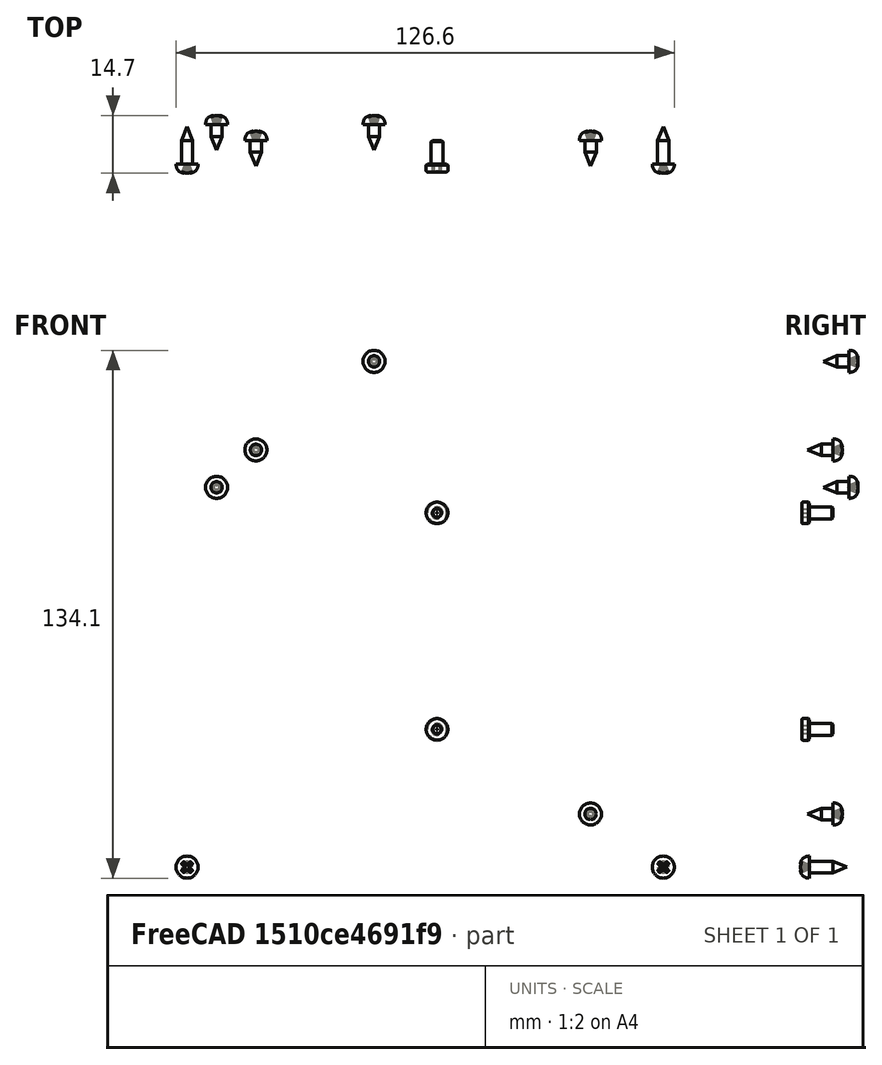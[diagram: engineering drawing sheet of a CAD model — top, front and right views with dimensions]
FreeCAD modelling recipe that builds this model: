
FCSTD DOCUMENT  (FreeCAD 1.0R39319 (Git))
Label: Assy_Stack_Module_PSU
License: All rights reserved
LicenseURL: https://en.wikipedia.org/wiki/All_rights_reserved
objects: TechDraw::DrawViewBalloon×18, App::Link×17, Part::FeaturePython×8, TechDraw::DrawProjGroupItem×6, TechDraw::DrawViewDimension×4, App::DocumentObjectGroup×3, TechDraw::DrawSVGTemplate×2, TechDraw::DrawPage×2, PartDesign::CoordinateSystem×1, App::FeaturePython×1, Spreadsheet::Sheet×1, TechDraw::DrawViewSpreadsheet×1, TechDraw::DrawViewAnnotation×1, App::Part×1, TechDraw::DrawProjGroup×1
note: 17 computed .brp shape members not serialized (recipe doc carries the construction recipe); baked Part::Feature solids carry a one-line shape summary decoded from their .brp
EXTERNAL_REF file=../../Part/Print/Stack_Module_PSU_vent.FCStd obj=LCS_1
EXTERNAL_REF file=../../Part/Print/Stack_Module_PSU_vent.FCStd obj=Part
EXTERNAL_REF file=Assy_M5_rod.FCStd obj=LCS_Origin
EXTERNAL_REF file=Assy_M5_rod.FCStd obj=Assembly
EXTERNAL_REF file=../../Part/Print/Stack_Module_PSU_vent.FCStd obj=LCS_2
EXTERNAL_REF file=../../Part/Print/Stack_Module_PSU_vent.FCStd obj=LCS_3
EXTERNAL_REF file=../../Part/Print/Stack_Module_PSU_vent.FCStd obj=LCS_4
EXTERNAL_REF file=../../Part/Print/Spacer.FCStd obj=LCS_1
EXTERNAL_REF file=../../Part/Print/Stack_Module_PSU_vent.FCStd obj=spacer_att
EXTERNAL_REF file=../../Part/Print/Spacer.FCStd obj=Part
EXTERNAL_REF file=../../Part/Print/Stack_Module_PSU_vent.FCStd obj=spacer_att_2
EXTERNAL_REF file=../../Part/Print/Stack_Module_PSU_vent.FCStd obj=spacer_att_3
EXTERNAL_REF file=../../Part/Print/Stack_Module_PSU_vent.FCStd obj=spacer_att_004
EXTERNAL_REF file=../../Part/Purchase/LRS-75.FCStd obj=stack_attach
EXTERNAL_REF file=../../Part/Print/Stack_Module_PSU_vent.FCStd obj=PSU_attachment
EXTERNAL_REF file=../../Part/Purchase/LRS-75.FCStd obj=LRS_75_ASM
EXTERNAL_REF file=Assy_Foot.FCStd obj=LCS_Origin
EXTERNAL_REF file=Assy_Foot.FCStd obj=Assembly
EXTERNAL_REF file=../../Part/Print/Ambient_LED_Screen.FCStd obj=stack_att
EXTERNAL_REF file=../../Part/Print/Stack_Module_PSU_vent.FCStd obj=screen_attachment
EXTERNAL_REF file=../../Part/Print/Ambient_LED_Screen.FCStd obj=Part
EXTERNAL_REF file=../../Part/Print/LinePower_Cover.FCStd obj=stack_att
EXTERNAL_REF file=../../Part/Print/Stack_Module_PSU_vent.FCStd obj=linecover_att
EXTERNAL_REF file=../../Part/Print/LinePower_Cover.FCStd obj=Part
EXTERNAL_REF file=../../Part/Print/Ambient_LED_Visor.FCStd obj=LCS_1
EXTERNAL_REF file=../../Part/Print/Ambient_LED_Visor.FCStd obj=Part

FEATURE [App::DocumentObjectGroup] Parts
FEATURE [PartDesign::CoordinateSystem] LCS_Origin
  AttacherType = Attacher::AttachEngine3D
  AttachmentSupport = -> [X_Axis]
  MapMode = 2
FEATURE [App::DocumentObjectGroup] Constraints
FEATURE [App::FeaturePython] Variables  # WARN: FeaturePython — macro-defined, semantics opaque (R4)
  Type = App::PropertyContainer
FEATURE [App::DocumentObjectGroup] Configurations
FEATURE [App::Link] Stack_Module_PSU_vent
  AttachedBy = #LCS_1
  AttachedTo = Parent Assembly#LCS_Origin
  AttachmentOffset = pos=(0,0,0) rot=(-0.57735,-0.57735,0.57735;4.18879rad)
  LinkPlacement = pos=(66.5,3.42e-14,53.5) rot=(0,0,1;3.14159rad)
  LinkedObject = -> <external ../../Part/Print/Stack_Module_PSU_vent.FCStd>#Part
  Placement = pos=(66.5,3.42e-14,53.5) rot=(0,0,1;3.14159rad)
  SolverId = Asm4EE
  expr: Placement = LCS_Origin.Placement * AttachmentOffset * Stack_Module_PSU_vent#LCS_1.Placement ^ -1
FEATURE [App::Link] Assy_M5_rod
  AttachedBy = #LCS_Origin
  AttachedTo = Stack_Module_PSU_vent#LCS_1
  AttachmentOffset = pos=(0,0,2) rot=(1,0,0;3.14159rad)
  LinkPlacement = pos=(1.49e-14,-2,1.47e-14) rot=(0.57735,-0.57735,-0.57735;4.18879rad)
  LinkedObject = -> <external Assy_M5_rod.FCStd>#Assembly
  Placement = pos=(1.49e-14,-2,1.47e-14) rot=(0.57735,-0.57735,-0.57735;4.18879rad)
  SolverId = Asm4EE
  expr: Placement = Stack_Module_PSU_vent.Placement * Stack_Module_PSU_vent#LCS_1.Placement * AttachmentOffset * Assy_M5_rod#LCS_Origin.Placement ^ -1
FEATURE [App::Link] Assy_M5_rod001
  AttachedBy = #LCS_Origin
  AttachedTo = Stack_Module_PSU_vent#LCS_2
  AttachmentOffset = pos=(0,0,2) rot=(1,0,0;3.14159rad)
  LinkPlacement = pos=(3,-2,116) rot=(0.57735,-0.57735,-0.57735;4.18879rad)
  LinkedObject = -> <external Assy_M5_rod.FCStd>#Assembly
  Placement = pos=(3,-2,116) rot=(0.57735,-0.57735,-0.57735;4.18879rad)
  SolverId = Asm4EE
  expr: Placement = Stack_Module_PSU_vent.Placement * Stack_Module_PSU_vent#LCS_2.Placement * AttachmentOffset * Assy_M5_rod#LCS_Origin.Placement ^ -1
FEATURE [App::Link] Assy_M5_rod002
  AttachedBy = #LCS_Origin
  AttachedTo = Stack_Module_PSU_vent#LCS_3
  AttachmentOffset = pos=(0,0,-2) rot=(0,0,1;0rad)
  LinkPlacement = pos=(133,-2,2.89e-14) rot=(-0.57735,0.57735,0.57735;2.0944rad)
  LinkedObject = -> <external Assy_M5_rod.FCStd>#Assembly
  Placement = pos=(133,-2,2.89e-14) rot=(-0.57735,0.57735,0.57735;2.0944rad)
  SolverId = Asm4EE
  expr: Placement = Stack_Module_PSU_vent.Placement * Stack_Module_PSU_vent#LCS_3.Placement * AttachmentOffset * Assy_M5_rod#LCS_Origin.Placement ^ -1
FEATURE [App::Link] Assy_M5_rod003
  AttachedBy = #LCS_Origin
  AttachedTo = Stack_Module_PSU_vent#LCS_4
  AttachmentOffset = pos=(0,0,-2) rot=(0,0,1;0rad)
  LinkPlacement = pos=(130,-2,116) rot=(-0.57735,0.57735,0.57735;2.0944rad)
  LinkedObject = -> <external Assy_M5_rod.FCStd>#Assembly
  Placement = pos=(130,-2,116) rot=(-0.57735,0.57735,0.57735;2.0944rad)
  SolverId = Asm4EE
  expr: Placement = Stack_Module_PSU_vent.Placement * Stack_Module_PSU_vent#LCS_4.Placement * AttachmentOffset * Assy_M5_rod#LCS_Origin.Placement ^ -1
FEATURE [App::Link] Spacer
  AttachedBy = #LCS_1
  AttachedTo = Stack_Module_PSU_vent#spacer_att
  LinkPlacement = pos=(0,35.25,7.1e-15) rot=(0,0.707107,0.707107;3.14159rad)
  LinkedObject = -> <external ../../Part/Print/Spacer.FCStd>#Part
  Placement = pos=(0,35.25,7.1e-15) rot=(0,0.707107,0.707107;3.14159rad)
  SolverId = Asm4EE
  expr: Placement = Stack_Module_PSU_vent.Placement * Stack_Module_PSU_vent#spacer_att.Placement * AttachmentOffset * Spacer#LCS_1.Placement ^ -1
FEATURE [App::Link] Spacer001
  AttachedBy = #LCS_1
  AttachedTo = Stack_Module_PSU_vent#spacer_att_2
  LinkPlacement = pos=(3,35.25,116) rot=(0,0.707107,0.707107;3.14159rad)
  LinkedObject = -> <external ../../Part/Print/Spacer.FCStd>#Part
  Placement = pos=(3,35.25,116) rot=(0,0.707107,0.707107;3.14159rad)
  SolverId = Asm4EE
  expr: Placement = Stack_Module_PSU_vent.Placement * Stack_Module_PSU_vent#spacer_att_2.Placement * AttachmentOffset * Spacer#LCS_1.Placement ^ -1
FEATURE [App::Link] Spacer002
  AttachedBy = #LCS_1
  AttachedTo = Stack_Module_PSU_vent#spacer_att_3
  AttachmentOffset = pos=(0,0,0) rot=(0,1,0;3.14159rad)
  LinkPlacement = pos=(130,35.25,116) rot=(1,0,0;4.71239rad)
  LinkedObject = -> <external ../../Part/Print/Spacer.FCStd>#Part
  Placement = pos=(130,35.25,116) rot=(1,0,0;4.71239rad)
  SolverId = Asm4EE
  expr: Placement = Stack_Module_PSU_vent.Placement * Stack_Module_PSU_vent#spacer_att_3.Placement * AttachmentOffset * Spacer#LCS_1.Placement ^ -1
FEATURE [App::Link] Spacer003
  AttachedBy = #LCS_1
  AttachedTo = Stack_Module_PSU_vent#spacer_att_004
  AttachmentOffset = pos=(0,0,0) rot=(0,1,0;3.14159rad)
  LinkPlacement = pos=(133,35.25,2.13e-14) rot=(1,0,0;4.71239rad)
  LinkedObject = -> <external ../../Part/Print/Spacer.FCStd>#Part
  Placement = pos=(133,35.25,2.13e-14) rot=(1,0,0;4.71239rad)
  SolverId = Asm4EE
  expr: Placement = Stack_Module_PSU_vent.Placement * Stack_Module_PSU_vent#spacer_att_004.Placement * AttachmentOffset * Spacer#LCS_1.Placement ^ -1
FEATURE [App::Link] LRS_75_ASM  label="LRS-75_ASM"
  AttachedBy = #stack_attach
  AttachedTo = Stack_Module_PSU_vent#PSU_attachment
  LinkPlacement = pos=(318.201,10.6,-201.167) rot=(-0.577138,0.577457,0.577457;2.09471rad)
  LinkedObject = -> <external ../../Part/Purchase/LRS-75.FCStd>#LRS_75_ASM
  Placement = pos=(318.201,10.6,-201.167) rot=(-0.577138,0.577457,0.577457;2.09471rad)
  SolverId = Asm4EE
  expr: Placement = Stack_Module_PSU_vent.Placement * Stack_Module_PSU_vent#PSU_attachment.Placement * AttachmentOffset * LRS_75#stack_attach.Placement ^ -1
FEATURE [App::Link] Assy_Foot
  AttachedBy = #LCS_Origin
  AttachedTo = Stack_Module_PSU_vent#LCS_1
  AttachmentOffset = pos=(0,0,5) rot=(0,1,0;3.14159rad)
  LinkPlacement = pos=(1.59e-14,-5,1.53e-14) rot=(0.57735,0.57735,0.57735;4.18879rad)
  LinkedObject = -> <external Assy_Foot.FCStd>#Assembly
  Placement = pos=(1.59e-14,-5,1.53e-14) rot=(0.57735,0.57735,0.57735;4.18879rad)
  SolverId = Asm4EE
  expr: Placement = Stack_Module_PSU_vent.Placement * Stack_Module_PSU_vent#LCS_1.Placement * AttachmentOffset * Assy_Foot#LCS_Origin.Placement ^ -1
FEATURE [App::Link] Assy_Foot001
  AttachedBy = #LCS_Origin
  AttachedTo = Stack_Module_PSU_vent#LCS_2
  AttachmentOffset = pos=(0,0,5) rot=(0,1,0;3.14159rad)
  LinkPlacement = pos=(3,-5,116) rot=(0.57735,0.57735,0.57735;4.18879rad)
  LinkedObject = -> <external Assy_Foot.FCStd>#Assembly
  Placement = pos=(3,-5,116) rot=(0.57735,0.57735,0.57735;4.18879rad)
  SolverId = Asm4EE
  expr: Placement = Stack_Module_PSU_vent.Placement * Stack_Module_PSU_vent#LCS_2.Placement * AttachmentOffset * Assy_Foot#LCS_Origin.Placement ^ -1
FEATURE [App::Link] Assy_Foot002
  AttachedBy = #LCS_Origin
  AttachedTo = Stack_Module_PSU_vent#LCS_3
  AttachmentOffset = pos=(0,0,-5) rot=(0,0,1;0rad)
  LinkPlacement = pos=(133,-5,2.95e-14) rot=(-0.57735,0.57735,0.57735;2.0944rad)
  LinkedObject = -> <external Assy_Foot.FCStd>#Assembly
  Placement = pos=(133,-5,2.95e-14) rot=(-0.57735,0.57735,0.57735;2.0944rad)
  SolverId = Asm4EE
  expr: Placement = Stack_Module_PSU_vent.Placement * Stack_Module_PSU_vent#LCS_3.Placement * AttachmentOffset * Assy_Foot#LCS_Origin.Placement ^ -1
FEATURE [App::Link] Assy_Foot003
  AttachedBy = #LCS_Origin
  AttachedTo = Stack_Module_PSU_vent#LCS_4
  AttachmentOffset = pos=(0,0,-5) rot=(0,0,1;0rad)
  LinkPlacement = pos=(130,-5,116) rot=(-0.57735,0.57735,0.57735;2.0944rad)
  LinkedObject = -> <external Assy_Foot.FCStd>#Assembly
  Placement = pos=(130,-5,116) rot=(-0.57735,0.57735,0.57735;2.0944rad)
  SolverId = Asm4EE
  expr: Placement = Stack_Module_PSU_vent.Placement * Stack_Module_PSU_vent#LCS_4.Placement * AttachmentOffset * Assy_Foot#LCS_Origin.Placement ^ -1
FEATURE [App::Link] Ambient_LED_Screen
  AttachedBy = #stack_att
  AttachedTo = Stack_Module_PSU_vent#screen_attachment
  LinkPlacement = pos=(66.5,3,-9) rot=(1,0,0;4.71239rad)
  LinkedObject = -> <external ../../Part/Print/Ambient_LED_Screen.FCStd>#Part
  Placement = pos=(66.5,3,-9) rot=(1,0,0;4.71239rad)
  SolverId = Asm4EE
  expr: Placement = Stack_Module_PSU_vent.Placement * Stack_Module_PSU_vent#screen_attachment.Placement * AttachmentOffset * Ambient_LED_Screen#stack_att.Placement ^ -1
FEATURE [App::Link] LinePower_Cover
  AttachedBy = #stack_att
  AttachedTo = Stack_Module_PSU_vent#linecover_att
  AttachmentOffset = pos=(0,0,0) rot=(0,0,1;3.14159rad)
  LinkPlacement = pos=(10.5,4,120.5) rot=(1,0,0;4.71239rad)
  LinkedObject = -> <external ../../Part/Print/LinePower_Cover.FCStd>#Part
  Placement = pos=(10.5,4,120.5) rot=(1,0,0;4.71239rad)
  SolverId = Asm4EE
  expr: Placement = Stack_Module_PSU_vent.Placement * Stack_Module_PSU_vent#linecover_att.Placement * AttachmentOffset * LinePower_Cover#stack_att.Placement ^ -1
FEATURE [Part::FeaturePython] Screw  label="ST2.9x6.5-Screw013"  # WARN: FeaturePython — macro-defined, semantics opaque (R4)
  BaseObject = -> Stack_Module_PSU_vent [Body.LinearPattern005.Edge4238]
  Diameter = 2
  Invert = false
  LeftHanded = false
  Length = 0
  LengthCustom = 6.5
  MatchOuter = false
  Offset = 2
  OffsetAngle = 0
  Placement = pos=(108.5,6,1.5) rot=(-1,0,0;1.5708rad)
  Thread = false
  Type = 81
FEATURE [Part::FeaturePython] Screw002  label="ST2.9x6.5-Screw"  # WARN: FeaturePython — macro-defined, semantics opaque (R4)
  BaseObject = -> Stack_Module_PSU_vent [Body.LinearPattern005.Edge4103]
  Diameter = 2
  Invert = false
  LeftHanded = false
  Length = 0
  LengthCustom = 6.5
  MatchOuter = false
  Offset = 2
  OffsetAngle = 0
  Placement = pos=(23.5,6,94) rot=(-1,0,0;1.5708rad)
  Thread = false
  Type = 81
FEATURE [Part::FeaturePython] Screw003  label="ST2.9x6.5-Screw014"  # WARN: FeaturePython — macro-defined, semantics opaque (R4)
  BaseObject = -> LinePower_Cover [Body.Fillet007.Edge85]
  Diameter = 2
  Invert = false
  LeftHanded = false
  Length = 0
  LengthCustom = 6.5
  MatchOuter = false
  OffsetAngle = 0
  Placement = pos=(53.5,10,116.5) rot=(-1,0,0;1.5708rad)
  Thread = false
  Type = 81
FEATURE [Part::FeaturePython] Screw004  label="ST2.9x6.5-Screw015"  # WARN: FeaturePython — macro-defined, semantics opaque (R4)
  BaseObject = -> LinePower_Cover [Body.Fillet007.Edge96]
  Diameter = 2
  Invert = false
  LeftHanded = false
  Length = 0
  LengthCustom = 6.5
  MatchOuter = false
  OffsetAngle = 0
  Placement = pos=(13.5,10,84.5) rot=(-1,0,0;1.5708rad)
  Thread = false
  Type = 81
FEATURE [Part::FeaturePython] Screw005  label="M3x6-Screw"  # WARN: FeaturePython — macro-defined, semantics opaque (R4)
  BaseObject = -> Stack_Module_PSU_vent [Body.LinearPattern005.Edge1214]
  Diameter = 1
  Invert = true
  LeftHanded = false
  Length = 1
  LengthCustom = 6
  MatchOuter = false
  OffsetAngle = 0
  Placement = pos=(69.5,2.01e-14,23) rot=(1,0,0;1.5708rad)
  Thread = false
  Type = 37
FEATURE [Part::FeaturePython] Screw006  label="M3x6-Screw001"  # WARN: FeaturePython — macro-defined, semantics opaque (R4)
  BaseObject = -> Stack_Module_PSU_vent [Body.LinearPattern005.Edge1213]
  Diameter = 1
  Invert = true
  LeftHanded = false
  Length = 1
  LengthCustom = 6
  MatchOuter = false
  OffsetAngle = 0
  Placement = pos=(69.5,4.1e-14,78) rot=(1,0,0;1.5708rad)
  Thread = false
  Type = 37
FEATURE [Part::FeaturePython] Screw007  label="ST2.9x9.5-Screw"  # WARN: FeaturePython — macro-defined, semantics opaque (R4)
  BaseObject = -> Stack_Module_PSU_vent [Body.LinearPattern005.Edge1216]
  Diameter = 2
  Invert = false
  LeftHanded = false
  Length = 1
  LengthCustom = 9.5
  MatchOuter = false
  OffsetAngle = 0
  Placement = pos=(127,2.26e-14,-12) rot=(1,0,0;1.5708rad)
  Thread = false
  Type = 81
FEATURE [Part::FeaturePython] Screw008  label="ST2.9x9.5-Screw001"  # WARN: FeaturePython — macro-defined, semantics opaque (R4)
  BaseObject = -> Stack_Module_PSU_vent [Body.LinearPattern005.Edge1215]
  Diameter = 2
  Invert = true
  LeftHanded = false
  Length = 1
  LengthCustom = 9.5
  MatchOuter = false
  OffsetAngle = 0
  Placement = pos=(6,-1.77e-14,-12) rot=(1,0,0;1.5708rad)
  Thread = false
  Type = 81
FEATURE [Spreadsheet::Sheet] Spreadsheet  label="BOM"
  cells = A1=12; B1=4; C1='M3x10 mm self-tapping screw; D1=' 5-16 mm; A2=11; B2=4; C2='M3x5 mm self-tapping screw; D2='5-6 mm; A3=10; B3=2; C3='M3x6 mm screw; D3='5-6 mm; A4=9; B4=3; C4='Wires; D4='-; A5=8; B5=1; C5='USB COB LED Strip Lights; D5='roughly 60 cm; A6=7; B6=1; C6='AC Power Inlet C14 with Fuse; D6='-; A7=6; B7=1; C7='Meanwell LRS-75-5; D7='-; A8=5; B8=4; C8='Spacer; D8='-; E8='PETG or PLA; A9=4; B9=1; C9='Ambient_LED_Visor; D9='-; E9='PETG or PLA; A10=3; B10=1; C10='LinePower_Cover; D10='-; E10='PETG or PLA; A11=2; B11=1; C11='Ambient_LED_Screen; D11='-; E11='PETG or PLA; A12=1; B12=1; C12='Stack_Module_PSU_vent; D12='-; E12='PETG or PLA; A13='Position; B13='Quantity; C13='Part; D13='Dimensions; E13='Material
FEATURE [TechDraw::DrawViewBalloon] Balloon
  BubbleShape = 0
  EndType = 0
  EndTypeScale = 1
  KinkLength = 5
  LockPosition = false
  OriginX = 74.9138
  OriginY = -16.347
  Rotation = 0
  ScaleType = 0
  ShapeScale = 1
  Text = 1
  TextWrapLen = -1
  X = 128.799
  Y = -72.3092
FEATURE [TechDraw::DrawViewBalloon] Balloon003
  BubbleShape = 0
  EndType = 0
  EndTypeScale = 1
  KinkLength = 5
  LockPosition = false
  OriginX = -3.65673
  OriginY = -43.3871
  Rotation = 0
  ScaleType = 0
  ShapeScale = 1
  Text = 4
  TextWrapLen = -1
  X = 130.81
  Y = -93.7522
FEATURE [TechDraw::DrawSVGTemplate] Template001
  EditableTexts = approval_person=GitHubPR; creator=Stefan; date_of_issue=19/3/2026; document_type=Assy_Stack_Module_PSU; general_tolerances=na; identification_number=na; language_code=EN; part_material=na; revision_index=AAA; scale=1 : 1; sheet_number=1 / 1; title=Assy_Stack_Module_PSU
  Height = 420
  Orientation = 1
  Template = <userpath>/Documents/PiTrac/3D Printed Parts/Enclosure Version 3/Assets/PiTrac_A2_Landscape_ISO5457_minimal.svg
  Width = 594
FEATURE [TechDraw::DrawViewSpreadsheet] Sheet001
  CellEnd = E13
  CellStart = A1
  Font = osifont
  LineWidth = 0.35
  LockPosition = false
  Rotation = 0
  ScaleType = 2
  Source = -> Spreadsheet
  Symbol = <blob: 14232 chars omitted>
  TextSize = 12
  X = 502.594
  Y = 129.653
FEATURE [TechDraw::DrawViewAnnotation] Annotation
  Font = osifont
  LineSpace = 100
  LockPosition = false
  MaxWidth = -1
  Rotation = 0
  ScaleType = 0
  Text = Not all parts are shown
  TextSize = 5
  TextStyle = 0
  X = 341.029
  Y = 39.0208
FEATURE [App::Link] Ambient_LED_Visor
  AttachedBy = #LCS_1
  AttachedTo = Parent Assembly#LCS_Origin
  AttachmentOffset = pos=(66.5,0,-46.5) rot=(0,0,1;3.14159rad)
  LinkPlacement = pos=(66.5,0,-46.5) rot=(0,0,1;3.14159rad)
  LinkedObject = -> <external ../../Part/Print/Ambient_LED_Visor.FCStd>#Part
  Placement = pos=(66.5,0,-46.5) rot=(0,0,1;3.14159rad)
  SolverId = Asm4EE
  expr: Placement = LCS_Origin.Placement * AttachmentOffset * Ambient_LED_Visor#LCS_1.Placement ^ -1
FEATURE [App::Part] Assembly  label="Assy_Stack_Module_PSU"
  AssemblyType = Part::Link
  Group = -> [LCS_Origin,Constraints,Variables,Configurations,Stack_Module_PSU_vent,Assy_M5_rod,Assy_M5_rod001,Assy_M5_rod002,Assy_M5_rod003,Spacer,Spacer001,Spacer002,Spacer003,LRS_75_ASM,Assy_Foot,Assy_Foot001,Assy_Foot002,Assy_Foot003,Ambient_LED_Screen,LinePower_Cover,Screw,Screw002,Screw003,Screw004,Screw005,Screw006,Screw007,Screw008,Ambient_LED_Visor]
  Origin = -> Origin
  Type = Assembly
FEATURE [TechDraw::DrawProjGroupItem] ProjItem  label="Top"
  CoarseView = false
  Direction = (0,1,0)
  Focus = 100
  HardHidden = false
  IsoCount = 0
  IsoHidden = false
  IsoVisible = false
  LockPosition = false
  Perspective = false
  Rotation = 0
  RotationVector = (1,0,0)
  ScaleType = 0
  ScrubCount = 1
  SeamHidden = false
  SeamVisible = false
  SmoothHidden = false
  SmoothVisible = true
  Source = -> [Assembly]
  Type = 4
  X = 0
  XDirection = (-1,0,-2e-16)
  Y = -133.625
FEATURE [TechDraw::DrawProjGroupItem] View002  label="Isometric View Scale 1:2"
  CoarseView = false
  Direction = (-0.57735,0.57735,-0.57735)
  Focus = 100
  HardHidden = false
  IsoCount = 0
  IsoHidden = false
  IsoVisible = false
  LockPosition = false
  Perspective = false
  Rotation = 0
  RotationVector = (1,0,0)
  Scale = 0.5
  ScaleType = 2
  ScrubCount = 1
  SeamHidden = false
  SeamVisible = false
  SmoothHidden = false
  SmoothVisible = true
  Source = -> [Assembly]
  Type = 0
  X = 336.894
  XDirection = (-0.707106,0,0.707106)
  Y = 114.331
FEATURE [TechDraw::DrawProjGroupItem] View003  label="Front001"
  CoarseView = false
  Direction = (0,0,-1)
  Focus = 100
  HardHidden = false
  IsoCount = 0
  IsoHidden = false
  IsoVisible = false
  LockPosition = true
  Perspective = false
  Rotation = 0
  RotationVector = (1,0,0)
  ScaleType = 2
  ScrubCount = 1
  SeamHidden = false
  SeamVisible = false
  SmoothHidden = false
  SmoothVisible = true
  Source = -> [Assembly]
  Type = 0
  X = 0
  XDirection = (-1,0,0)
  Y = 0
FEATURE [TechDraw::DrawProjGroupItem] ProjItem002  label="Top001"
  CoarseView = false
  Direction = (0,1,0)
  Focus = 100
  HardHidden = false
  IsoCount = 0
  IsoHidden = false
  IsoVisible = false
  LockPosition = false
  Perspective = false
  Rotation = 0
  RotationVector = (1,0,0)
  ScaleType = 0
  ScrubCount = 1
  SeamHidden = false
  SeamVisible = false
  SmoothHidden = false
  SmoothVisible = true
  Source = -> [Assembly]
  Type = 4
  X = 0
  XDirection = (-1,0,0)
  Y = -132.298
FEATURE [TechDraw::DrawProjGroupItem] ProjItem003  label="Left001"
  CoarseView = false
  Direction = (1,0,-1e-16)
  Focus = 100
  HardHidden = false
  IsoCount = 0
  IsoHidden = false
  IsoVisible = false
  LockPosition = false
  Perspective = false
  Rotation = 0
  RotationVector = (1,0,0)
  ScaleType = 0
  ScrubCount = 1
  SeamHidden = false
  SeamVisible = false
  SmoothHidden = false
  SmoothVisible = true
  Source = -> [Assembly]
  Type = 1
  X = 187
  XDirection = (-1e-16,0,-1)
  Y = 0
FEATURE [TechDraw::DrawProjGroup] ProjGroup001
  Anchor = -> View003
  AutoDistribute = true
  LockPosition = false
  ProjectionType = 0
  Rotation = 0
  ScaleType = 0
  Source = -> [Assembly]
  Views = -> [View003,ProjItem002,ProjItem003]
  X = 154.029
  Y = 330.521
  spacingX = 15
  spacingY = 15
FEATURE [TechDraw::DrawViewBalloon] Balloon007
  BubbleShape = 0
  EndType = 0
  EndTypeScale = 1
  KinkLength = 5
  LockPosition = false
  OriginX = -59
  OriginY = 9.65153
  Rotation = 0
  ScaleType = 0
  ShapeScale = 1
  SourceView = -> ProjItem002
  Text = 1
  TextWrapLen = -1
  X = -100
  Y = 25.036
FEATURE [TechDraw::DrawViewBalloon] Balloon008
  BubbleShape = 0
  EndType = 0
  EndTypeScale = 1
  KinkLength = 5
  LockPosition = false
  OriginX = -39.6652
  OriginY = 0.173159
  Rotation = 0
  ScaleType = 0
  ShapeScale = 1
  SourceView = -> View003
  Text = 2
  TextWrapLen = -1
  X = -100
  Y = 15.5576
FEATURE [TechDraw::DrawViewBalloon] Balloon009
  BubbleShape = 0
  EndType = 0
  EndTypeScale = 1
  KinkLength = 5
  LockPosition = false
  OriginX = 32.6431
  OriginY = 50.5032
  Rotation = 0
  ScaleType = 0
  ShapeScale = 1
  SourceView = -> ProjItem002
  Text = 3
  TextWrapLen = -1
  X = 100
  Y = 58.1951
FEATURE [TechDraw::DrawViewBalloon] Balloon010
  BubbleShape = 0
  EndType = 0
  EndTypeScale = 1
  KinkLength = 5
  LockPosition = false
  OriginX = -44.7952
  OriginY = -78.7316
  Rotation = 0
  ScaleType = 0
  ShapeScale = 1
  SourceView = -> ProjItem002
  Text = 4
  TextWrapLen = -1
  X = -100
  Y = -60.2701
FEATURE [TechDraw::DrawViewBalloon] Balloon011
  BubbleShape = 0
  EndType = 0
  EndTypeScale = 1
  KinkLength = 5
  LockPosition = false
  OriginX = -63.25
  OriginY = -48.5
  Rotation = 0
  ScaleType = 0
  ShapeScale = 1
  SourceView = -> ProjItem002
  Text = 5
  TextWrapLen = -1
  X = -100
  Y = -23.3716
FEATURE [TechDraw::DrawViewBalloon] Balloon012
  BubbleShape = 0
  EndType = 0
  EndTypeScale = 1
  KinkLength = 5
  LockPosition = false
  OriginX = -59.1546
  OriginY = 67.9396
  Rotation = 0
  ScaleType = 0
  ShapeScale = 1
  SourceView = -> ProjItem002
  Text = 5
  TextWrapLen = -1
  X = -100
  Y = 85
FEATURE [TechDraw::DrawViewBalloon] Balloon014
  BubbleShape = 0
  EndType = 0
  EndTypeScale = 1
  KinkLength = 5
  LockPosition = false
  OriginX = 62.9004
  OriginY = 64.8626
  Rotation = 0
  ScaleType = 0
  ShapeScale = 1
  SourceView = -> ProjItem002
  Text = 5
  TextWrapLen = -1
  X = 99.4872
  Y = 83.9743
FEATURE [TechDraw::DrawViewBalloon] Balloon015
  BubbleShape = 0
  EndType = 0
  EndTypeScale = 1
  KinkLength = 5
  LockPosition = false
  OriginX = 64.4389
  OriginY = -46.4229
  Rotation = 0
  ScaleType = 0
  ShapeScale = 1
  SourceView = -> ProjItem002
  Text = 5
  TextWrapLen = -1
  X = 100
  Y = -30.5256
FEATURE [TechDraw::DrawViewBalloon] Balloon016
  BubbleShape = 0
  EndType = 0
  EndTypeScale = 1
  KinkLength = 5
  LockPosition = false
  OriginX = 19.8222
  OriginY = 26.3999
  Rotation = 0
  ScaleType = 0
  ShapeScale = 1
  SourceView = -> ProjItem002
  Text = 6
  TextWrapLen = -1
  X = 100
  Y = 14.604
FEATURE [TechDraw::DrawViewBalloon] Balloon017
  BubbleShape = 0
  EndType = 0
  EndTypeScale = 1
  KinkLength = 5
  LockPosition = false
  OriginX = -26.75
  OriginY = -21.6518
  Rotation = 0
  ScaleType = 0
  ShapeScale = 1
  SourceView = -> ProjItem003
  Text = 10
  TextWrapLen = -1
  X = -42.1357
  Y = -49
FEATURE [TechDraw::DrawViewBalloon] Balloon018
  BubbleShape = 0
  EndType = 0
  EndTypeScale = 1
  KinkLength = 5
  LockPosition = false
  OriginX = 28.7257
  OriginY = -22.306
  Rotation = 0
  ScaleType = 0
  ShapeScale = 1
  SourceView = -> ProjItem003
  Text = 10
  TextWrapLen = -1
  X = 47.7
  Y = -49
FEATURE [TechDraw::DrawViewBalloon] Balloon019
  BubbleShape = 0
  EndType = 0
  EndTypeScale = 1
  KinkLength = 5
  LockPosition = false
  OriginX = -61.2512
  OriginY = -22.105
  Rotation = 0
  ScaleType = 0
  ShapeScale = 1
  SourceView = -> View003
  Text = 12
  TextWrapLen = -1
  X = -100
  Y = -14.4131
FEATURE [TechDraw::DrawViewBalloon] Balloon020
  BubbleShape = 0
  EndType = 0
  EndTypeScale = 1
  KinkLength = 5
  LockPosition = false
  OriginX = 61.2512
  OriginY = -22.105
  Rotation = 0
  ScaleType = 0
  ShapeScale = 1
  SourceView = -> View003
  Text = 12
  TextWrapLen = -1
  X = 122.791
  Y = -49
FEATURE [TechDraw::DrawViewBalloon] Balloon021
  BubbleShape = 0
  EndType = 0
  EndTypeScale = 1
  KinkLength = 5
  LockPosition = false
  OriginX = 12.4289
  OriginY = 67.795
  Rotation = 0
  ScaleType = 0
  ShapeScale = 1
  SourceView = -> ProjItem002
  Text = 11
  TextWrapLen = -1
  X = -100
  Y = 101.947
FEATURE [TechDraw::DrawViewBalloon] Balloon022
  BubbleShape = 0
  EndType = 0
  EndTypeScale = 1
  KinkLength = 5
  LockPosition = false
  OriginX = 53.6694
  OriginY = 36.1438
  Rotation = 0
  ScaleType = 0
  ShapeScale = 1
  SourceView = -> ProjItem002
  Text = 11
  TextWrapLen = -1
  X = 100
  Y = 36.7508
FEATURE [TechDraw::DrawViewBalloon] Balloon024
  BubbleShape = 0
  EndType = 0
  EndTypeScale = 1
  KinkLength = 5
  LockPosition = false
  OriginX = -40.504
  OriginY = -48.9784
  Rotation = 0
  ScaleType = 0
  ShapeScale = 1
  SourceView = -> ProjItem002
  Text = 11
  TextWrapLen = -1
  X = -100
  Y = -0.151091
FEATURE [TechDraw::DrawViewDimension] Dimension001
  AngleOverride = false
  Arbitrary = false
  ArbitraryTolerances = false
  BoxCorners = (2) [(-95,-22.2982,-1e-07),(95,22.2982,1e-07)]
  EqualTolerance = true
  ExtensionAngle = 0
  FormatSpec = %.2w
  FormatSpecOverTolerance = %+.2w
  FormatSpecUnderTolerance = %+.2w
  Inverted = false
  LineAngle = 0
  LockPosition = false
  MeasureType = 1
  OverTolerance = 0
  References2D = -> [ProjItem003]
  Rotation = 0
  ScaleType = 0
  TheoreticalExact = false
  Type = 1
  UnderTolerance = 0
  X = 0
  Y = 40
FEATURE [TechDraw::DrawViewDimension] Dimension002
  AngleOverride = false
  Arbitrary = false
  ArbitraryTolerances = false
  BoxCorners = (2) [(-77,-22.2982,-1e-07),(77,22.2982,1e-07)]
  EqualTolerance = true
  ExtensionAngle = 0
  FormatSpec = %.2w
  FormatSpecOverTolerance = %+.2w
  FormatSpecUnderTolerance = %+.2w
  Inverted = false
  LineAngle = 0
  LockPosition = false
  MeasureType = 1
  OverTolerance = 0
  References2D = -> [View003]
  Rotation = 0
  ScaleType = 0
  TheoreticalExact = false
  Type = 1
  UnderTolerance = 0
  X = 0
  Y = 40
FEATURE [TechDraw::DrawViewDimension] Dimension003
  AngleOverride = false
  Arbitrary = false
  ArbitraryTolerances = false
  BoxCorners = (2) [(-95,-22.2982,-1e-07),(95,22.2982,1e-07)]
  EqualTolerance = true
  ExtensionAngle = 0
  FormatSpec = %.2w
  FormatSpecOverTolerance = %+.2w
  FormatSpecUnderTolerance = %+.2w
  Inverted = false
  LineAngle = 0
  LockPosition = false
  MeasureType = 1
  OverTolerance = 0
  References2D = -> [ProjItem003]
  Rotation = 0
  ScaleType = 0
  TheoreticalExact = false
  Type = 0
  UnderTolerance = 0
  X = 131.873
  Y = 0.173159
FEATURE [TechDraw::DrawViewDimension] Dimension004
  AngleOverride = false
  Arbitrary = false
  ArbitraryTolerances = false
  BoxCorners = (2) [(-95,-22.2982,-1e-07),(95,22.2982,1e-07)]
  EqualTolerance = true
  ExtensionAngle = 0
  FormatSpec = %.2w
  FormatSpecOverTolerance = %+.2w
  FormatSpecUnderTolerance = %+.2w
  Inverted = false
  LineAngle = 0
  LockPosition = false
  MeasureType = 1
  OverTolerance = 0
  References2D = -> [ProjItem003]
  Rotation = 0
  ScaleType = 0
  TheoreticalExact = false
  Type = 2
  UnderTolerance = 0
  X = 160.232
  Y = 0.323159
FEATURE [TechDraw::DrawPage] Page001
  KeepUpdated = true
  NextBalloonIndex = 21
  ProjectionType = 0
  Template = -> Template001
  Views = -> [View002,Sheet001,ProjGroup001,Balloon007,Balloon008,Balloon009,Balloon010,Balloon011,Balloon012,Balloon014,Balloon015,Balloon016,Balloon017,Balloon018,Balloon019,Balloon020,Balloon021,Balloon022,Balloon024,Dimension001,Dimension002,Dimension003,Dimension004,Annotation]
FEATURE [TechDraw::DrawSVGTemplate] Template
  Height = 210
  Orientation = 1
  Template = C:/Program Files/FreeCAD 1.0/data/Mod/TechDraw/Templates/Default_Template_A4_Landscape.svg
  Width = 297
FEATURE [TechDraw::DrawProjGroupItem] View
  CoarseView = false
  Direction = (-0.57735,0.57735,-0.57735)
  Focus = 100
  HardHidden = false
  IsoCount = 0
  IsoHidden = false
  IsoVisible = false
  LockPosition = false
  Perspective = false
  Rotation = 0
  RotationVector = (1,0,0)
  ScaleType = 0
  ScrubCount = 1
  SeamHidden = false
  SeamVisible = false
  SmoothHidden = false
  SmoothVisible = true
  Source = -> [Assembly]
  Type = 0
  X = 148.5
  XDirection = (-0.707106,0,0.707106)
  Y = 105
FEATURE [TechDraw::DrawPage] Page
  KeepUpdated = true
  NextBalloonIndex = 1
  ProjectionType = 0
  Template = -> Template
  Views = -> [View]

RESOLVED EXTERNAL PARTS (link-assembly join: the EXTERNAL_REF files above that resolve inside this repo's crawl, each included once):
---- part ../../Part/Print/Ambient_LED_Screen.FCStd = doc fcstd_3e985b0e07c3 ----
FCSTD DOCUMENT  (FreeCAD 1.0R39319 (Git))
Label: Ambient_LED_Screen
License: All rights reserved
LicenseURL: https://en.wikipedia.org/wiki/All_rights_reserved
objects: Sketcher::SketchObject×7, PartDesign::Pocket×5, PartDesign::Pad×2, PartDesign::Chamfer×1, PartDesign::Mirrored×1, PartDesign::Body×1, PartDesign::CoordinateSystem×1, App::Part×1
note: 42 computed .brp shape members not serialized (recipe doc carries the construction recipe); baked Part::Feature solids carry a one-line shape summary decoded from their .brp

FEATURE [Sketcher::SketchObject] Sketch
  ArcFitTolerance = 1e-06
  AttachmentSupport = -> [XY_Plane001]
  FullyConstrained = true
  MakeInternals = false
  MapMode = 5
  sketch-geometry (20):
    g0: LineSegment StartX=52.3059 StartY=0 StartZ=0 EndX=60.5 EndY=0 EndZ=0
    g1: ArcOfCircle CenterX=60.5 CenterY=3 CenterZ=0 NormalX=0 NormalY=0 NormalZ=1 AngleXU=0 Radius=3 StartAngle=4.71239 EndAngle=8.29889
    g2: LineSegment StartX=59.2089 StartY=5.70795 StartZ=0 EndX=48.6478 EndY=0.672534 EndZ=0
    g3: ArcOfCircle CenterX=0 CenterY=4.259 CenterZ=0 NormalX=0 NormalY=0 NormalZ=1 AngleXU=0 Radius=7 StartAngle=4.71239 EndAngle=5.61581
    g4: ArcOfCircle CenterX=0 CenterY=4.259 CenterZ=0 NormalX=0 NormalY=0 NormalZ=1 AngleXU=0 Radius=5.5 StartAngle=4.71239 EndAngle=5.61581
    g5: LineSegment StartX=-1.3e-15 StartY=-2.741 StartZ=0 EndX=-1.3e-15 EndY=-1.241 EndZ=0
    g6: ArcOfCircle CenterX=10.9963 CenterY=-4.40596 CenterZ=0 NormalX=0 NormalY=0 NormalZ=1 AngleXU=0 Radius=7 StartAngle=0.667374 EndAngle=2.47422
    g7: ArcOfCircle CenterX=10.9963 CenterY=-4.40596 CenterZ=0 NormalX=0 NormalY=0 NormalZ=1 AngleXU=0 Radius=8.5 StartAngle=0.667374 EndAngle=2.47422
    g8: ArcOfCircle CenterX=21.9926 CenterY=4.259 CenterZ=0 NormalX=0 NormalY=0 NormalZ=1 AngleXU=0 Radius=5.5 StartAngle=3.80897 EndAngle=5.61581
    g9: ArcOfCircle CenterX=21.9926 CenterY=4.259 CenterZ=0 NormalX=0 NormalY=0 NormalZ=1 AngleXU=0 Radius=7 StartAngle=3.80897 EndAngle=5.61581
    g10: ArcOfCircle CenterX=32.9889 CenterY=-4.40596 CenterZ=0 NormalX=0 NormalY=0 NormalZ=1 AngleXU=0 Radius=8.5 StartAngle=0.667374 EndAngle=2.47422
    g11: ArcOfCircle CenterX=32.9889 CenterY=-4.40596 CenterZ=0 NormalX=0 NormalY=0 NormalZ=1 AngleXU=0 Radius=7 StartAngle=0.667374 EndAngle=2.47422
    g12: ArcOfCircle CenterX=43.9852 CenterY=4.259 CenterZ=0 NormalX=0 NormalY=0 NormalZ=1 AngleXU=0 Radius=7 StartAngle=3.80897 EndAngle=5.34883
    g13: ArcOfCircle CenterX=43.9852 CenterY=4.259 CenterZ=0 NormalX=0 NormalY=0 NormalZ=1 AngleXU=0 Radius=5.5 StartAngle=3.80897 EndAngle=5.34883
    g14: ArcOfCircle CenterX=52.3059 CenterY=-7 CenterZ=0 NormalX=0 NormalY=0 NormalZ=1 AngleXU=0 Radius=8.5 StartAngle=2.0157 EndAngle=2.20724
    g15: ArcOfCircle CenterX=52.3059 CenterY=-7 CenterZ=0 NormalX=0 NormalY=0 NormalZ=1 AngleXU=0 Radius=7 StartAngle=1.5708 EndAngle=2.20724
    g16: GeomPoint [constr] X=66 Y=10 Z=0
    g17: LineSegment [constr] StartX=48.1455 StartY=-1.3705 StartZ=0 EndX=50 EndY=2e-16 EndZ=0
    g18: LineSegment [constr] StartX=10.9963 StartY=-4.40596 StartZ=0 EndX=32.9889 EndY=-4.40596 EndZ=0
    g19: LineSegment [constr] StartX=0 StartY=4.259 StartZ=0 EndX=43.9852 EndY=4.259 EndZ=0
  constraints (49):
    c: PointOnObject(g0,g-1)
    c: PointOnObject(g0,g-1)
    c: Tangent(g0,g1) = -1.5708
    c: Tangent(g1,g2) = -1.5708
    c: Coincident(g5,g3)
    c: Coincident(g5,g4)
    c: Vertical(g5)
    c: Coincident(g4,g3)
    c: PointOnObject(g3,g-2)
    c: Tangent(g6,g3) = 1.5708
    c: Tangent(g7,g4) = 1.5708
    c: Coincident(g6,g7)
    c: Radius(g6) = 7
    c: Distance(g5,g5) = 1.5
    c: Tangent(g8,g7) = 1.5708
    c: Tangent(g9,g6) = 1.5708
    c: Coincident(g9,g8)
    c: PointOnObject(g3,g-2)
    c: Tangent(g10,g8) = 1.5708
    c: Tangent(g11,g9) = 1.5708
    c: Coincident(g11,g10)
    c: Tangent(g12,g11) = 1.5708
    c: Tangent(g13,g10) = 1.5708
    c: Coincident(g12,g13)
    c: Tangent(g14,g13) = 1.5708
    c: Tangent(g14,g2) = -1.5708
    c: Tangent(g15,g0) = 1.5708
    c: Radius(g9) = 7
    c: Radius(g12) = 7
    c: Coincident(g15,g14)
    c: DistanceX(g-1,g16) = 66
    c: Distance(g16,g-1) = 10
    c: Radius(g1) = 3
    c: Distance(g1,g-2) = 60.5
    c: Tangent(g15,g12) = 1.5708
    c: Tangent(g12,g17) = -1.5708
    c: Radius(g3) = 7
    c: Radius(g11) = 7
    c: Radius(g15) = 7
    c: PointOnObject(g17,g-1)
    c: DistanceX(g-1,g17) = 50
    c: Coincident(g18,g6)
    c: Coincident(g18,g10)
    c: Coincident(g19,g3)
    c: Coincident(g19,g12)
    c: Horizontal(g19)
    c: PointOnObject(g8,g19)
    c: Horizontal(g18)
    c: Distance(g-1,g19) = 4.259
FEATURE [PartDesign::Pad] Pad
  Direction = (0,0,1)
  Length = 34.25
  Length2 = 10
  Profile = -> Sketch
  ReferenceAxis = -> Sketch [N_Axis]
  Refine = true
  Suppressed = false
  Type = 0
FEATURE [Sketcher::SketchObject] Sketch001
  ArcFitTolerance = 1e-06
  AttachmentSupport = -> [Pad]
  ExternalGeometry = -> [Pad]
  FullyConstrained = true
  MakeInternals = false
  MapMode = 5
  Placement = pos=(0,0,0) rot=(1,0,0;3.14159rad)
  sketch-geometry (1):
    g0: Circle CenterX=60.5 CenterY=-3 CenterZ=0 NormalX=0 NormalY=0 NormalZ=1 AngleXU=0 Radius=1.25
  constraints (2):
    c: Coincident(g0,g-3)
    c: Diameter(g0) = 2.5
FEATURE [PartDesign::Pocket] Pocket
  BaseFeature = -> Pad
  Direction = (0,0,1)
  Length = 10
  Length2 = 5
  Profile = -> Sketch001
  ReferenceAxis = -> Sketch001 [N_Axis]
  Refine = true
  Suppressed = false
  Type = 0
FEATURE [Sketcher::SketchObject] Sketch002
  ArcFitTolerance = 1e-06
  AttachmentSupport = -> [Pocket]
  FullyConstrained = true
  MakeInternals = false
  MapMode = 5
  Placement = pos=(0,0,34.25) rot=(0,0,1;0rad)
  sketch-geometry (4):
    g0: LineSegment StartX=0 StartY=7.59 StartZ=0 EndX=0 EndY=-5.3 EndZ=0
    g1: LineSegment StartX=0 StartY=-5.3 StartZ=0 EndX=70.5 EndY=-5.3 EndZ=0
    g2: LineSegment StartX=70.5 StartY=-5.3 StartZ=0 EndX=70.5 EndY=7.59 EndZ=0
    g3: LineSegment StartX=70.5 StartY=7.59 StartZ=0 EndX=0 EndY=7.59 EndZ=0
  constraints (12):
    c: Coincident(g0,g1)
    c: Coincident(g1,g2)
    c: Coincident(g2,g3)
    c: Coincident(g3,g0)
    c: Vertical(g0)
    c: Vertical(g2)
    c: Horizontal(g1)
    c: Horizontal(g3)
    c: PointOnObject(g0,g-2)
    c: Distance(g2,g0) = 70.5
    c: Distance(g3,g1) = 12.89
    c: Distance(g1,g-1) = 5.3
FEATURE [PartDesign::Pad] Pad001
  BaseFeature = -> Pocket
  Direction = (0,0,1)
  Length = 3
  Length2 = 10
  Profile = -> Sketch002
  ReferenceAxis = -> Sketch002 [N_Axis]
  Refine = true
  Suppressed = false
  Type = 0
FEATURE [Sketcher::SketchObject] Sketch003
  ArcFitTolerance = 1e-06
  AttachmentSupport = -> [Pad001]
  ExternalGeometry = -> [Pad001]
  FullyConstrained = true
  MakeInternals = false
  MapMode = 5
  Placement = pos=(0,0,37.25) rot=(0,0,1;0rad)
  sketch-geometry (4):
    g0: LineSegment StartX=70.5 StartY=-2.5 StartZ=0 EndX=55.5 EndY=-2.5 EndZ=0
    g1: LineSegment StartX=55.5 StartY=-2.5 StartZ=0 EndX=55.5 EndY=-5.3 EndZ=0
    g2: LineSegment StartX=55.5 StartY=-5.3 StartZ=0 EndX=70.5 EndY=-5.3 EndZ=0
    g3: LineSegment StartX=70.5 StartY=-5.3 StartZ=0 EndX=70.5 EndY=-2.5 EndZ=0
  constraints (12):
    c: Coincident(g0,g1)
    c: Coincident(g1,g2)
    c: Coincident(g2,g3)
    c: Coincident(g3,g0)
    c: Horizontal(g0)
    c: Horizontal(g2)
    c: Vertical(g1)
    c: Vertical(g3)
    c: PointOnObject(g0,g-3)
    c: PointOnObject(g1,g-4)
    c: Distance(g3,g1) = 15
    c: Distance(g2,g0) = 2.8
FEATURE [PartDesign::Pocket] Pocket001
  BaseFeature = -> Pad001
  Direction = (0,0,-1)
  Length = 5
  Length2 = 5
  Profile = -> Sketch003
  ReferenceAxis = -> Sketch003 [N_Axis]
  Refine = true
  Suppressed = false
  Type = 1
FEATURE [Sketcher::SketchObject] Sketch004
  ArcFitTolerance = 1e-06
  AttachmentSupport = -> [Pocket001]
  ExternalGeometry = -> [Pocket001]
  FullyConstrained = true
  MakeInternals = false
  MapMode = 5
  Placement = pos=(0,0,37.25) rot=(0,0,1;0rad)
  sketch-geometry (4):
    g0: LineSegment StartX=65.5 StartY=7.59 StartZ=0 EndX=65.5 EndY=4.09 EndZ=0
    g1: LineSegment StartX=65.5 StartY=4.09 StartZ=0 EndX=70.5 EndY=4.09 EndZ=0
    g2: LineSegment StartX=70.5 StartY=4.09 StartZ=0 EndX=70.5 EndY=7.59 EndZ=0
    g3: LineSegment StartX=70.5 StartY=7.59 StartZ=0 EndX=65.5 EndY=7.59 EndZ=0
  constraints (12):
    c: Coincident(g0,g1)
    c: Coincident(g1,g2)
    c: Coincident(g2,g3)
    c: Coincident(g3,g0)
    c: Vertical(g0)
    c: Vertical(g2)
    c: Horizontal(g1)
    c: Horizontal(g3)
    c: PointOnObject(g0,g-4)
    c: Distance(g2,g0) = 5
    c: Distance(g1,g3) = 3.5
    c: PointOnObject(g1,g-3)
FEATURE [PartDesign::Pocket] Pocket002
  BaseFeature = -> Pocket001
  Direction = (0,0,-1)
  Length = 5
  Length2 = 5
  Profile = -> Sketch004
  ReferenceAxis = -> Sketch004 [N_Axis]
  Refine = true
  Suppressed = false
  Type = 1
FEATURE [Sketcher::SketchObject] Sketch005
  ArcFitTolerance = 1e-06
  AttachmentSupport = -> [Pocket002]
  ExternalGeometry = -> [Pocket002]
  FullyConstrained = true
  MakeInternals = false
  MapMode = 5
  Placement = pos=(0,0,37.25) rot=(0,0,1;0rad)
  sketch-geometry (1):
    g0: Circle CenterX=68 CenterY=1 CenterZ=0 NormalX=0 NormalY=0 NormalZ=1 AngleXU=0 Radius=1.5
  constraints (3):
    c: Distance(g0,g-2) = 68
    c: Distance(g0,g-3) = 3.5
    c: Diameter(g0) = 3
FEATURE [PartDesign::Pocket] Pocket003
  BaseFeature = -> Pocket002
  Direction = (0,0,-1)
  Length = 5
  Length2 = 5
  Profile = -> Sketch005
  ReferenceAxis = -> Sketch005 [N_Axis]
  Refine = true
  Suppressed = false
  Type = 1
FEATURE [Sketcher::SketchObject] Sketch006
  ArcFitTolerance = 1e-06
  AttachmentSupport = -> [Pocket003]
  ExternalGeometry = -> [Pocket003]
  FullyConstrained = true
  MakeInternals = false
  MapMode = 5
  Placement = pos=(0,0,37.25) rot=(0,0,1;0rad)
  sketch-geometry (2):
    g0: Circle CenterX=65.5 CenterY=4.09 CenterZ=0 NormalX=0 NormalY=0 NormalZ=1 AngleXU=0 Radius=0.5
    g1: Circle CenterX=55.5 CenterY=-2.5 CenterZ=0 NormalX=0 NormalY=0 NormalZ=1 AngleXU=0 Radius=0.5
  constraints (4):
    c: Coincident(g0,g-3)
    c: Coincident(g1,g-4)
    c: Diameter(g0) = 1
    c: Diameter(g1) = 1
FEATURE [PartDesign::Pocket] Pocket004
  BaseFeature = -> Pocket003
  Direction = (0,0,-1)
  Length = 5
  Length2 = 5
  Profile = -> Sketch006
  ReferenceAxis = -> Sketch006 [N_Axis]
  Refine = true
  Suppressed = false
  Type = 1
FEATURE [PartDesign::Chamfer] Chamfer
  Angle = 45
  Base = -> Pocket004 [Edge81,Edge68]
  BaseFeature = -> Pocket004
  ChamferType = 0
  FlipDirection = false
  Refine = true
  Size = 0.5
  Size2 = 1
  SupportTransform = false
  Suppressed = false
  UseAllEdges = false
FEATURE [PartDesign::Mirrored] Mirrored
  BaseFeature = -> Chamfer
  MirrorPlane = -> YZ_Plane001
  Refine = true
  Suppressed = false
  TransformMode = 1
FEATURE [PartDesign::Body] Body  label="Ambient_LED_Screen001"
  AllowCompound = false
  Group = -> [Sketch,Pad,Sketch001,Pocket,Sketch002,Pad001,Sketch003,Pocket001,Sketch004,Pocket002,Sketch005,Pocket003,Sketch006,Pocket004,Chamfer,Mirrored]
  Origin = -> Origin001
  Tip = -> Mirrored
FEATURE [PartDesign::CoordinateSystem] stack_att
  AttacherType = Attacher::AttachEngine3D
  AttachmentSupport = -> [Mirrored]
  MapMode = 11
  Placement = pos=(60.5,3,0) rot=(0.707107,-0.707107,0;3.14159rad)
FEATURE [App::Part] Part  label="Ambient_LED_Screen"
  Group = -> [Body,stack_att]
  Origin = -> Origin
---- part ../../Part/Print/Ambient_LED_Visor.FCStd = doc fcstd_8e89421252ca ----
FCSTD DOCUMENT  (FreeCAD 1.0R39319 (Git))
Label: Ambient_LED_Visor
License: All rights reserved
LicenseURL: https://en.wikipedia.org/wiki/All_rights_reserved
objects: Sketcher::SketchObject×4, PartDesign::Fillet×3, PartDesign::Pad×2, PartDesign::Pocket×2, PartDesign::CoordinateSystem×1, PartDesign::Mirrored×1, PartDesign::Body×1, App::Part×1
note: 33 computed .brp shape members not serialized (recipe doc carries the construction recipe); baked Part::Feature solids carry a one-line shape summary decoded from their .brp

FEATURE [Sketcher::SketchObject] Sketch
  ArcFitTolerance = 1e-06
  AttachmentSupport = -> [XZ_Plane001]
  FullyConstrained = false
  MakeInternals = false
  MapMode = 5
  Placement = pos=(0,0,0) rot=(1,0,0;1.5708rad)
  sketch-geometry (10):
    g0: LineSegment StartX=0 StartY=30 StartZ=0 EndX=74 EndY=30 EndZ=0
    g1: LineSegment StartX=74 StartY=30 StartZ=0 EndX=74 EndY=46.75 EndZ=0
    g2: ArcOfCircle CenterX=66.5 CenterY=46.75 CenterZ=0 NormalX=0 NormalY=0 NormalZ=1 AngleXU=0 Radius=7.5 StartAngle=0 EndAngle=1.5708
    g3: LineSegment [constr] StartX=66.5 StartY=46.75 StartZ=0 EndX=66.5 EndY=54.25 EndZ=0
    g4: LineSegment StartX=0 StartY=30 StartZ=0 EndX=0 EndY=0 EndZ=0
    g5: LineSegment StartX=0 StartY=0 StartZ=0 EndX=77 EndY=0 EndZ=0
    g6: LineSegment StartX=77 StartY=0 StartZ=0 EndX=77 EndY=46.75 EndZ=0
    g7: ArcOfCircle CenterX=66.5 CenterY=55.75 CenterZ=0 NormalX=0 NormalY=0 NormalZ=1 AngleXU=0 Radius=1.5 StartAngle=1.5708 EndAngle=4.71239
    g8: ArcOfCircle CenterX=66.5 CenterY=46.75 CenterZ=0 NormalX=0 NormalY=0 NormalZ=1 AngleXU=0 Radius=10.5 StartAngle=0 EndAngle=1.5708
    g9: GeomPoint [constr] X=77 Y=60.25 Z=0
  constraints (25):
    c: PointOnObject(g0,g-2)
    c: Horizontal(g0)
    c: Coincident(g0,g1)
    c: Vertical(g1)
    c: Tangent(g1,g2) = -1.5708
    c: DistanceX(g0,g0) = 74
    c: Distance(g2,g0) = 16.75
    c: Radius(g2) = 7.5
    c: Coincident(g3,g2)
    c: Coincident(g3,g2)
    c: Vertical(g3)
    c: Coincident(g0,g4)
    c: Coincident(g4,g-1)
    c: Coincident(g4,g5)
    c: PointOnObject(g5,g-1)
    c: Coincident(g5,g6)
    c: Vertical(g6)
    c: Coincident(g7,g2)
    c: Distance(g6,g1) = 3
    c: Distance(g5,g0) = 30
    c: PointOnObject(g7,g3)
    c: PointOnObject(g9,g6)
    c: Tangent(g6,g8) = -1.5708
    c: Tangent(g7,g8) = -1.5708
    c: Coincident(g2,g8)
FEATURE [PartDesign::Pad] Pad
  Direction = (0,-1,2e-16)
  Length = 40.25
  Length2 = 10
  Placement = pos=(0,0,0) rot=(1,0,0;1.5708rad)
  Profile = -> Sketch
  ReferenceAxis = -> Sketch [N_Axis]
  Refine = true
  Suppressed = false
  Type = 0
FEATURE [Sketcher::SketchObject] Sketch001
  ArcFitTolerance = 1e-06
  AttachmentSupport = -> [Pad]
  ExternalGeometry = -> [Pad]
  FullyConstrained = true
  MakeInternals = false
  MapMode = 5
  Placement = pos=(0,4.9e-15,0) rot=(-1,0,0;1.5708rad)
  sketch-geometry (4):
    g0: LineSegment StartX=0 StartY=0 StartZ=0 EndX=0 EndY=-30 EndZ=0
    g1: LineSegment StartX=0 StartY=-30 StartZ=0 EndX=74 EndY=-30 EndZ=0
    g2: LineSegment StartX=74 StartY=-30 StartZ=0 EndX=74 EndY=0 EndZ=0
    g3: LineSegment StartX=74 StartY=0 StartZ=0 EndX=0 EndY=0 EndZ=0
  constraints (10):
    c: Coincident(g0,g1)
    c: Coincident(g1,g2)
    c: Coincident(g2,g3)
    c: Coincident(g3,g0)
    c: Vertical(g0)
    c: Vertical(g2)
    c: Horizontal(g1)
    c: Horizontal(g3)
    c: Coincident(g0,g-1)
    c: Coincident(g1,g-5)
FEATURE [PartDesign::Fillet] Fillet001
  Base = -> Pad [Edge17]
  BaseFeature = -> Pad
  Placement = pos=(0,0,0) rot=(1,0,0;1.5708rad)
  Radius = 7.5
  Refine = true
  SupportTransform = false
  Suppressed = false
  UseAllEdges = false
FEATURE [PartDesign::Pocket] Pocket
  BaseFeature = -> Fillet001
  Direction = (0,-1,-2e-16)
  Length = 0
  Length2 = 5
  Offset = -3
  Placement = pos=(0,0,0) rot=(1,0,0;1.5708rad)
  Profile = -> Sketch001
  ReferenceAxis = -> Sketch001 [N_Axis]
  Refine = true
  Suppressed = false
  Type = 3
  UpToFace = -> Pad [Face10]
FEATURE [Sketcher::SketchObject] Sketch002
  ArcFitTolerance = 1e-06
  AttachmentSupport = -> [Fillet001]
  ExternalGeometry = -> [Fillet001]
  FullyConstrained = true
  MakeInternals = false
  MapMode = 5
  Placement = pos=(74,0,0) rot=(0.707107,0,-0.707107;3.14159rad)
  sketch-geometry (6):
    g0: LineSegment StartX=-46.75 StartY=0 StartZ=0 EndX=0 EndY=0 EndZ=0
    g1: LineSegment StartX=0 StartY=0 StartZ=0 EndX=0 EndY=37.25 EndZ=0
    g2: LineSegment StartX=-41.4698 StartY=2.17372 StartZ=0 EndX=-8.28022 EndY=35.0763 EndZ=0
    g3: ArcOfCircle CenterX=-3 CenterY=29.75 CenterZ=0 NormalX=0 NormalY=0 NormalZ=1 AngleXU=0 Radius=7.5 StartAngle=1.5708 EndAngle=2.35185
    g4: ArcOfCircle CenterX=-46.75 CenterY=7.5 CenterZ=0 NormalX=0 NormalY=0 NormalZ=1 AngleXU=0 Radius=7.5 StartAngle=4.71239 EndAngle=5.49344
    g5: LineSegment StartX=-3 StartY=37.25 StartZ=0 EndX=0 EndY=37.25 EndZ=0
  constraints (15):
    c: Coincident(g0,g-1)
    c: Coincident(g0,g1)
    c: Distance(g1,g-3) = 3
    c: PointOnObject(g0,g-1)
    c: PointOnObject(g0,g-4)
    c: Tangent(g3,g2) = 1.5708
    c: Tangent(g4,g2) = -1.5708
    c: Tangent(g4,g0) = -1.5708
    c: Radius(g4) = 7.5
    c: PointOnObject(g1,g-2)
    c: Coincident(g5,g1)
    c: Horizontal(g5)
    c: Tangent(g5,g3) = 1.5708
    c: DistanceX(g5,g5) = 3
    c: Radius(g3) = 7.5
FEATURE [PartDesign::Pocket] Pocket001
  BaseFeature = -> Pocket
  Direction = (1,0,2e-16)
  Length = 5
  Length2 = 5
  Midplane = true
  Placement = pos=(0,0,0) rot=(1,0,0;1.5708rad)
  Profile = -> Sketch002
  ReferenceAxis = -> Sketch002 [N_Axis]
  Refine = true
  Suppressed = false
  Type = 1
FEATURE [PartDesign::CoordinateSystem] LCS_1
  AttacherType = Attacher::AttachEngine3D
FEATURE [Sketcher::SketchObject] Sketch003
  ArcFitTolerance = 1e-06
  AttachmentSupport = -> [Pocket001]
  ExternalGeometry = -> [Pocket001]
  FullyConstrained = true
  MakeInternals = false
  MapMode = 5
  Placement = pos=(0,-37.25,1.79e-14) rot=(-1,0,0;1.5708rad)
  sketch-geometry (4):
    g0: LineSegment StartX=66 StartY=-27 StartZ=0 EndX=66 EndY=-30 EndZ=0
    g1: LineSegment StartX=66 StartY=-30 StartZ=0 EndX=74 EndY=-30 EndZ=0
    g2: LineSegment StartX=74 StartY=-30 StartZ=0 EndX=74 EndY=-27 EndZ=0
    g3: LineSegment StartX=74 StartY=-27 StartZ=0 EndX=66 EndY=-27 EndZ=0
  constraints (11):
    c: Coincident(g0,g1)
    c: Coincident(g1,g2)
    c: Coincident(g2,g3)
    c: Coincident(g3,g0)
    c: Vertical(g0)
    c: Vertical(g2)
    c: Horizontal(g1)
    c: Horizontal(g3)
    c: Distance(g1,g3) = 3
    c: Distance(g2,g0) = 8
    c: Coincident(g1,g-3)
FEATURE [PartDesign::Pad] Pad001
  BaseFeature = -> Pocket001
  Direction = (0,1,2e-16)
  Length = 10
  Length2 = 10
  Placement = pos=(0,0,0) rot=(1,0,0;1.5708rad)
  Profile = -> Sketch003
  ReferenceAxis = -> Sketch003 [N_Axis]
  Refine = true
  Suppressed = false
  Type = 3
  UpToFace = -> Pocket001 [Face6]
FEATURE [PartDesign::Fillet] Fillet
  Base = -> Pad001 [Edge35]
  BaseFeature = -> Pad001
  Placement = pos=(0,0,0) rot=(1,0,0;1.5708rad)
  Radius = 2.5
  Refine = true
  SupportTransform = false
  Suppressed = false
  UseAllEdges = false
FEATURE [PartDesign::Fillet] Fillet002
  Base = -> Fillet [Edge46]
  BaseFeature = -> Fillet
  Placement = pos=(0,0,0) rot=(1,0,0;1.5708rad)
  Radius = 7.5
  Refine = true
  SupportTransform = false
  Suppressed = false
  UseAllEdges = false
FEATURE [PartDesign::Mirrored] Mirrored
  BaseFeature = -> Fillet002
  MirrorPlane = -> YZ_Plane001
  Placement = pos=(0,0,0) rot=(1,0,0;1.5708rad)
  Refine = true
  Suppressed = false
  TransformMode = 1
FEATURE [PartDesign::Body] Body  label="Ambient_LED_Visor001"
  AllowCompound = false
  Group = -> [Sketch,Pad,Fillet001,Sketch001,Pocket,Sketch002,Pocket001,Sketch003,Pad001,Fillet,Fillet002,Mirrored]
  Origin = -> Origin001
  Tip = -> Mirrored
FEATURE [App::Part] Part  label="Ambient_LED_Visor"
  Group = -> [Body,LCS_1]
  Origin = -> Origin
---- part ../../Part/Print/LinePower_Cover.FCStd = doc fcstd_72adacda487f ----
FCSTD DOCUMENT  (FreeCAD 1.0R39319 (Git))
Label: LinePower_Cover
License: All rights reserved
LicenseURL: https://en.wikipedia.org/wiki/All_rights_reserved
objects: Sketcher::SketchObject×12, PartDesign::Pocket×9, PartDesign::Fillet×8, PartDesign::Pad×3, PartDesign::Body×1, PartDesign::CoordinateSystem×1, App::Part×1
note: 86 computed .brp shape members not serialized (recipe doc carries the construction recipe); baked Part::Feature solids carry a one-line shape summary decoded from their .brp

FEATURE [Sketcher::SketchObject] Sketch
  ArcFitTolerance = 1e-06
  AttachmentSupport = -> [XY_Plane001]
  FullyConstrained = true
  MakeInternals = false
  MapMode = 5
  sketch-geometry (4):
    g0: LineSegment StartX=0 StartY=0 StartZ=0 EndX=49 EndY=0 EndZ=0
    g1: LineSegment StartX=49 StartY=0 StartZ=0 EndX=49 EndY=40 EndZ=0
    g2: LineSegment StartX=49 StartY=40 StartZ=0 EndX=0 EndY=40 EndZ=0
    g3: LineSegment StartX=0 StartY=40 StartZ=0 EndX=0 EndY=0 EndZ=0
  constraints (11):
    c: Coincident(g0,g1)
    c: Coincident(g1,g2)
    c: Coincident(g2,g3)
    c: Coincident(g3,g0)
    c: Horizontal(g0)
    c: Horizontal(g2)
    c: Vertical(g1)
    c: Vertical(g3)
    c: Coincident(g0,g-1)
    c: Distance(g0,g2) = 40
    c: Distance(g1,g3) = 49
FEATURE [PartDesign::Pad] Pad
  Direction = (0,0,1)
  Length = 33
  Length2 = 10
  Profile = -> Sketch
  ReferenceAxis = -> Sketch [N_Axis]
  Refine = true
  Suppressed = false
  Type = 0
FEATURE [Sketcher::SketchObject] Sketch001
  ArcFitTolerance = 1e-06
  AttachmentSupport = -> [XY_Plane001]
  ExternalGeometry = -> [Pad]
  FullyConstrained = true
  MakeInternals = false
  MapMode = 5
  sketch-geometry (4):
    g0: LineSegment StartX=0 StartY=0 StartZ=0 EndX=47 EndY=0 EndZ=0
    g1: LineSegment StartX=47 StartY=0 StartZ=0 EndX=47 EndY=21 EndZ=0
    g2: LineSegment StartX=47 StartY=21 StartZ=0 EndX=0 EndY=21 EndZ=0
    g3: LineSegment StartX=0 StartY=21 StartZ=0 EndX=0 EndY=0 EndZ=0
  constraints (11):
    c: Coincident(g0,g1)
    c: Coincident(g1,g2)
    c: Coincident(g2,g3)
    c: Coincident(g3,g0)
    c: Horizontal(g0)
    c: Horizontal(g2)
    c: Vertical(g1)
    c: Vertical(g3)
    c: Coincident(g0,g-1)
    c: Distance(g0,g2) = 21
    c: Distance(g-3,g1) = 2
FEATURE [PartDesign::Pocket] Pocket
  BaseFeature = -> Pad
  Direction = (0,0,-1)
  Length = 31
  Length2 = 5
  Profile = -> Sketch001
  ReferenceAxis = -> Sketch001 [N_Axis]
  Refine = true
  Reversed = true
  Suppressed = false
  Type = 0
FEATURE [Sketcher::SketchObject] Sketch002
  ArcFitTolerance = 1e-06
  AttachmentSupport = -> [Pocket]
  ExternalGeometry = -> [Pocket]
  FullyConstrained = true
  MakeInternals = false
  MapMode = 5
  Placement = pos=(0,0,0) rot=(1,0,0;3.14159rad)
  sketch-geometry (4):
    g0: LineSegment StartX=7 StartY=-40 StartZ=0 EndX=49 EndY=-40 EndZ=0
    g1: LineSegment StartX=49 StartY=-40 StartZ=0 EndX=49 EndY=-21 EndZ=0
    g2: LineSegment StartX=49 StartY=-21 StartZ=0 EndX=7 EndY=-21 EndZ=0
    g3: LineSegment StartX=7 StartY=-21 StartZ=0 EndX=7 EndY=-40 EndZ=0
  constraints (12):
    c: Coincident(g0,g1)
    c: Coincident(g1,g2)
    c: Coincident(g2,g3)
    c: Coincident(g3,g0)
    c: Horizontal(g0)
    c: Horizontal(g2)
    c: Vertical(g1)
    c: Vertical(g3)
    c: PointOnObject(g0,g-4)
    c: PointOnObject(g-3,g2)
    c: Distance(g3,g-2) = 7
    c: PointOnObject(g-5,g1)
FEATURE [PartDesign::Pocket] Pocket001
  BaseFeature = -> Pocket
  Direction = (0,0,1)
  Length = 31
  Length2 = 5
  Profile = -> Sketch002
  ReferenceAxis = -> Sketch002 [N_Axis]
  Refine = true
  Suppressed = false
  Type = 0
FEATURE [Sketcher::SketchObject] Sketch003
  ArcFitTolerance = 1e-06
  AttachmentSupport = -> [Pocket001]
  ExternalGeometry = -> [Pocket001]
  FullyConstrained = true
  MakeInternals = false
  MapMode = 5
  Placement = pos=(0,0,0) rot=(1,0,0;3.14159rad)
  sketch-geometry (4):
    g0: LineSegment StartX=7 StartY=-21 StartZ=0 EndX=0 EndY=-21 EndZ=0
    g1: LineSegment StartX=0 StartY=-21 StartZ=0 EndX=0 EndY=-28 EndZ=0
    g2: LineSegment StartX=0 StartY=-28 StartZ=0 EndX=7 EndY=-28 EndZ=0
    g3: LineSegment StartX=7 StartY=-28 StartZ=0 EndX=7 EndY=-21 EndZ=0
  constraints (11):
    c: Coincident(g0,g1)
    c: Coincident(g1,g2)
    c: Coincident(g2,g3)
    c: Coincident(g3,g0)
    c: Horizontal(g0)
    c: Horizontal(g2)
    c: Vertical(g1)
    c: Vertical(g3)
    c: Coincident(g0,g-4)
    c: PointOnObject(g1,g-2)
    c: Distance(g-1,g2) = 28
FEATURE [PartDesign::Pocket] Pocket002
  BaseFeature = -> Pocket001
  Direction = (0,0,1)
  Length = 31
  Length2 = 5
  Profile = -> Sketch003
  ReferenceAxis = -> Sketch003 [N_Axis]
  Refine = true
  Suppressed = false
  Type = 0
FEATURE [Sketcher::SketchObject] Sketch004
  ArcFitTolerance = 1e-06
  AttachmentSupport = -> [Pocket002]
  ExternalGeometry = -> [Pocket002]
  FullyConstrained = true
  MakeInternals = false
  MapMode = 5
  Placement = pos=(0,0,31) rot=(1,0,0;3.14159rad)
  sketch-geometry (4):
    g0: LineSegment StartX=47 StartY=0 StartZ=0 EndX=37 EndY=0 EndZ=0
    g1: LineSegment StartX=37 StartY=0 StartZ=0 EndX=37 EndY=-10 EndZ=0
    g2: LineSegment StartX=37 StartY=-10 StartZ=0 EndX=47 EndY=-10 EndZ=0
    g3: LineSegment StartX=47 StartY=-10 StartZ=0 EndX=47 EndY=0 EndZ=0
  constraints (11):
    c: Coincident(g0,g1)
    c: Coincident(g1,g2)
    c: Coincident(g2,g3)
    c: Coincident(g3,g0)
    c: Horizontal(g0)
    c: Horizontal(g2)
    c: Vertical(g1)
    c: Vertical(g3)
    c: Coincident(g0,g-3)
    c: Distance(g0,g2) = 10
    c: Distance(g3,g1) = 10
FEATURE [PartDesign::Pad] Pad001
  BaseFeature = -> Pocket002
  Direction = (0,0,-1)
  Length = 27
  Length2 = 10
  Profile = -> Sketch004
  ReferenceAxis = -> Sketch004 [N_Axis]
  Refine = true
  Suppressed = false
  Type = 0
FEATURE [Sketcher::SketchObject] Sketch005
  ArcFitTolerance = 1e-06
  AttachmentSupport = -> [Pad001]
  ExternalGeometry = -> [Pad001]
  FullyConstrained = true
  MakeInternals = false
  MapMode = 5
  Placement = pos=(0,0,33) rot=(0,0,1;0rad)
  sketch-geometry (4):
    g0: LineSegment StartX=49 StartY=0 StartZ=0 EndX=49 EndY=8 EndZ=0
    g1: LineSegment StartX=49 StartY=8 StartZ=0 EndX=39 EndY=8 EndZ=0
    g2: LineSegment StartX=39 StartY=8 StartZ=0 EndX=39 EndY=0 EndZ=0
    g3: LineSegment StartX=39 StartY=0 StartZ=0 EndX=49 EndY=0 EndZ=0
  constraints (11):
    c: Coincident(g0,g1)
    c: Coincident(g1,g2)
    c: Coincident(g2,g3)
    c: Coincident(g3,g0)
    c: Vertical(g0)
    c: Vertical(g2)
    c: Horizontal(g1)
    c: Horizontal(g3)
    c: Coincident(g0,g-3)
    c: Distance(g-5,g1) = 2
    c: Distance(g-4,g2) = 2
FEATURE [PartDesign::Pocket] Pocket003
  BaseFeature = -> Pad001
  Direction = (0,0,-1)
  Length = 0
  Length2 = 5
  Offset = -2
  Profile = -> Sketch005
  ReferenceAxis = -> Sketch005 [N_Axis]
  Refine = true
  Suppressed = false
  Type = 3
  UpToFace = -> Pad001 [Face14]
FEATURE [Sketcher::SketchObject] Sketch006
  ArcFitTolerance = 1e-06
  AttachmentSupport = -> [Pocket003]
  ExternalGeometry = -> [Pocket003]
  FullyConstrained = true
  MakeInternals = false
  MapMode = 5
  Placement = pos=(0,0,0) rot=(1,0,0;3.14159rad)
  sketch-geometry (4):
    g0: LineSegment StartX=7 StartY=-28 StartZ=0 EndX=0 EndY=-28 EndZ=0
    g1: LineSegment StartX=0 StartY=-28 StartZ=0 EndX=0 EndY=-40 EndZ=0
    g2: LineSegment StartX=0 StartY=-40 StartZ=0 EndX=7 EndY=-40 EndZ=0
    g3: LineSegment StartX=7 StartY=-40 StartZ=0 EndX=7 EndY=-28 EndZ=0
  constraints (10):
    c: Coincident(g0,g1)
    c: Coincident(g1,g2)
    c: Coincident(g2,g3)
    c: Coincident(g3,g0)
    c: Horizontal(g0)
    c: Horizontal(g2)
    c: Vertical(g1)
    c: Vertical(g3)
    c: Coincident(g0,g-4)
    c: Coincident(g1,g-5)
FEATURE [PartDesign::Pocket] Pocket004
  BaseFeature = -> Pocket003
  Direction = (0,0,1)
  Length = 0
  Length2 = 5
  Profile = -> Sketch006
  ReferenceAxis = -> Sketch006 [N_Axis]
  Refine = true
  Suppressed = false
  Type = 3
  UpToFace = -> Pocket003 [Face18]
FEATURE [Sketcher::SketchObject] Sketch007
  ArcFitTolerance = 1e-06
  AttachmentSupport = -> [Pocket004]
  ExternalGeometry = -> [Pocket004]
  FullyConstrained = true
  MakeInternals = false
  MapMode = 5
  Placement = pos=(0,0,33) rot=(0,0,1;0rad)
  sketch-geometry (4):
    g0: LineSegment StartX=0 StartY=40 StartZ=0 EndX=0 EndY=30 EndZ=0
    g1: LineSegment StartX=0 StartY=30 StartZ=0 EndX=5 EndY=30 EndZ=0
    g2: LineSegment StartX=5 StartY=30 StartZ=0 EndX=5 EndY=40 EndZ=0
    g3: LineSegment StartX=5 StartY=40 StartZ=0 EndX=0 EndY=40 EndZ=0
  constraints (11):
    c: Coincident(g0,g1)
    c: Coincident(g1,g2)
    c: Coincident(g2,g3)
    c: Coincident(g3,g0)
    c: Vertical(g0)
    c: Vertical(g2)
    c: Horizontal(g1)
    c: Horizontal(g3)
    c: Coincident(g0,g-3)
    c: Distance(g-5,g2) = 2
    c: Distance(g-4,g1) = 2
FEATURE [PartDesign::Pocket] Pocket005
  BaseFeature = -> Pocket004
  Direction = (0,0,-1)
  Length = 0
  Length2 = 5
  Offset = -2
  Profile = -> Sketch007
  ReferenceAxis = -> Sketch007 [N_Axis]
  Refine = true
  Suppressed = false
  Type = 3
  UpToFace = -> Pocket004 [Face2]
FEATURE [PartDesign::Fillet] Fillet
  Base = -> Pocket005 [Edge55]
  BaseFeature = -> Pocket005
  Radius = 4
  Refine = true
  SupportTransform = false
  Suppressed = false
  UseAllEdges = false
FEATURE [Sketcher::SketchObject] Sketch008
  ArcFitTolerance = 1e-06
  AttachmentSupport = -> [Fillet]
  ExternalGeometry = -> [Fillet]
  FullyConstrained = true
  MakeInternals = false
  MapMode = 5
  Placement = pos=(0,0,6) rot=(0,0,1;0rad)
  sketch-geometry (1):
    g0: Circle CenterX=43 CenterY=4 CenterZ=0 NormalX=0 NormalY=0 NormalZ=1 AngleXU=0 Radius=1.6
  constraints (3):
    c: Diameter(g0) = 3.2
    c: Distance(g0,g-4) = 4
    c: Distance(g0,g-3) = 4
FEATURE [PartDesign::Pocket] Pocket006
  BaseFeature = -> Fillet
  Direction = (0,0,-1)
  Length = 5
  Length2 = 5
  Profile = -> Sketch008
  ReferenceAxis = -> Sketch008 [N_Axis]
  Refine = true
  Suppressed = false
  Type = 1
FEATURE [Sketcher::SketchObject] Sketch009
  ArcFitTolerance = 1e-06
  AttachmentSupport = -> [Pocket006]
  FullyConstrained = true
  MakeInternals = false
  MapMode = 5
  Placement = pos=(0,0,6) rot=(0,0,1;0rad)
  sketch-geometry (1):
    g0: Circle CenterX=3 CenterY=36 CenterZ=0 NormalX=0 NormalY=0 NormalZ=1 AngleXU=0 Radius=1.6
  constraints (3):
    c: Diameter(g0) = 3.2
    c: DistanceY(g-1,g0) = 36
    c: Distance(g0,g-2) = 3
FEATURE [PartDesign::Pocket] Pocket007
  BaseFeature = -> Pocket006
  Direction = (0,0,-1)
  Length = 5
  Length2 = 5
  Profile = -> Sketch009
  ReferenceAxis = -> Sketch009 [N_Axis]
  Refine = true
  Suppressed = false
  Type = 1
FEATURE [Sketcher::SketchObject] Sketch010
  ArcFitTolerance = 1e-06
  AttachmentSupport = -> [Pocket007]
  ExternalGeometry = -> [Pocket007]
  FullyConstrained = true
  MakeInternals = false
  MapMode = 5
  Placement = pos=(0,0,33) rot=(0,0,1;0rad)
  sketch-geometry (1):
    g0: Circle CenterX=3 CenterY=36 CenterZ=0 NormalX=0 NormalY=0 NormalZ=1 AngleXU=0 Radius=2.75
  constraints (2):
    c: Coincident(g0,g-3)
    c: Diameter(g0) = 5.5
FEATURE [PartDesign::Pocket] Pocket008
  BaseFeature = -> Pocket007
  Direction = (0,0,-1)
  Length = 0
  Length2 = 5
  Profile = -> Sketch010
  ReferenceAxis = -> Sketch010 [N_Axis]
  Refine = true
  Suppressed = false
  Type = 3
  UpToFace = -> Pocket007 [Face16]
FEATURE [PartDesign::Fillet] Fillet001
  Base = -> Pocket008 [Edge32]
  BaseFeature = -> Pocket008
  Radius = 2
  Refine = true
  SupportTransform = false
  Suppressed = false
  UseAllEdges = false
FEATURE [PartDesign::Fillet] Fillet002
  Base = -> Fillet001 [Edge44]
  BaseFeature = -> Fillet001
  Radius = 4
  Refine = true
  SupportTransform = false
  Suppressed = false
  UseAllEdges = false
FEATURE [Sketcher::SketchObject] Sketch011
  ArcFitTolerance = 1e-06
  AttachmentSupport = -> [Fillet002]
  ExternalGeometry = -> [Fillet002]
  FullyConstrained = true
  MakeInternals = false
  MapMode = 5
  Placement = pos=(49,0,0) rot=(0.57735,0.57735,0.57735;2.0944rad)
  sketch-geometry (4):
    g0: LineSegment StartX=21 StartY=31 StartZ=0 EndX=21 EndY=22.5 EndZ=0
    g1: LineSegment StartX=21 StartY=22.5 StartZ=0 EndX=32.5 EndY=22.5 EndZ=0
    g2: LineSegment StartX=32.5 StartY=22.5 StartZ=0 EndX=32.5 EndY=31 EndZ=0
    g3: LineSegment StartX=32.5 StartY=31 StartZ=0 EndX=21 EndY=31 EndZ=0
  constraints (11):
    c: Coincident(g0,g1)
    c: Coincident(g1,g2)
    c: Coincident(g2,g3)
    c: Coincident(g3,g0)
    c: Vertical(g0)
    c: Vertical(g2)
    c: Horizontal(g1)
    c: Horizontal(g3)
    c: Coincident(g0,g-4)
    c: Distance(g2,g0) = 11.5
    c: Distance(g1,g-1) = 22.5
FEATURE [PartDesign::Pad] Pad002
  BaseFeature = -> Fillet002
  Direction = (1,0,0)
  Length = 10
  Length2 = 10
  Profile = -> Sketch011
  ReferenceAxis = -> Sketch011 [N_Axis]
  Refine = true
  Suppressed = false
  Type = 3
  UpToFace = -> Fillet002 [Face22]
FEATURE [PartDesign::Fillet] Fillet003
  Base = -> Pad002 [Edge3,Edge65]
  BaseFeature = -> Pad002
  Radius = 2
  Refine = true
  SupportTransform = false
  Suppressed = false
  UseAllEdges = false
FEATURE [PartDesign::Fillet] Fillet004
  Base = -> Fillet003 [Edge72]
  BaseFeature = -> Fillet003
  Radius = 4
  Refine = true
  SupportTransform = false
  Suppressed = false
  UseAllEdges = false
FEATURE [PartDesign::Fillet] Fillet005
  Base = -> Fillet004 [Edge57]
  BaseFeature = -> Fillet004
  Radius = 6
  Refine = true
  SupportTransform = false
  Suppressed = false
  UseAllEdges = false
FEATURE [PartDesign::Fillet] Fillet006
  Base = -> Fillet005 [Edge27]
  BaseFeature = -> Fillet005
  Radius = 2
  Refine = true
  SupportTransform = false
  Suppressed = false
  UseAllEdges = false
FEATURE [PartDesign::Fillet] Fillet007
  Base = -> Fillet006 [Edge33]
  BaseFeature = -> Fillet006
  Radius = 2
  Refine = true
  SupportTransform = false
  Suppressed = false
  UseAllEdges = false
FEATURE [PartDesign::Body] Body  label="LinePower_Cover001"
  AllowCompound = false
  Group = -> [Sketch,Pad,Sketch001,Pocket,Sketch002,Pocket001,Sketch003,Pocket002,Sketch004,Pad001,Sketch005,Pocket003,Sketch006,Pocket004,Sketch007,Pocket005,Fillet,Sketch008,Pocket006,Sketch009,Pocket007,Sketch010,Pocket008,Fillet001,Fillet002,Sketch011,Pad002,Fillet003,Fillet004,Fillet005,Fillet006,Fillet007]
  Origin = -> Origin001
  Tip = -> Fillet007
FEATURE [PartDesign::CoordinateSystem] stack_att
  AttacherType = Attacher::AttachEngine3D
  AttachmentSupport = -> [Fillet007]
  MapMode = 11
  Placement = pos=(43,4,4) rot=(0,0,1;1.5708rad)
FEATURE [App::Part] Part  label="LinePower_Cover"
  Group = -> [Body,stack_att]
  Origin = -> Origin
---- part ../../Part/Print/Spacer.FCStd = doc fcstd_2f39e15fa6d1 ----
FCSTD DOCUMENT  (FreeCAD 1.0R39319 (Git))
Label: Spacer
License: All rights reserved
LicenseURL: https://en.wikipedia.org/wiki/All_rights_reserved
objects: Sketcher::SketchObject×1, PartDesign::Pad×1, PartDesign::Chamfer×1, PartDesign::Body×1, PartDesign::CoordinateSystem×1, App::Part×1
note: 10 computed .brp shape members not serialized (recipe doc carries the construction recipe); baked Part::Feature solids carry a one-line shape summary decoded from their .brp

FEATURE [Sketcher::SketchObject] Sketch
  ArcFitTolerance = 1e-06
  AttachmentSupport = -> [XY_Plane001]
  FullyConstrained = true
  MakeInternals = false
  MapMode = 5
  sketch-geometry (2):
    g0: Circle CenterX=0 CenterY=0 CenterZ=0 NormalX=0 NormalY=0 NormalZ=1 AngleXU=0 Radius=4.25
    g1: Circle CenterX=0 CenterY=0 CenterZ=0 NormalX=0 NormalY=0 NormalZ=1 AngleXU=0 Radius=3.25
  constraints (4):
    c: Coincident(g0,g-1)
    c: Coincident(g1,g0)
    c: Diameter(g1) = 6.5
    c: Diameter(g0) = 8.5
FEATURE [PartDesign::Pad] Pad
  Direction = (0,0,1)
  Length = 7
  Length2 = 10
  Profile = -> Sketch
  ReferenceAxis = -> Sketch [N_Axis]
  Refine = true
  Suppressed = false
  Type = 0
FEATURE [PartDesign::Chamfer] Chamfer
  Angle = 45
  Base = -> Pad [Edge3,Edge2]
  BaseFeature = -> Pad
  ChamferType = 0
  FlipDirection = false
  Refine = true
  Size = 0.25
  Size2 = 1
  SupportTransform = false
  Suppressed = false
  UseAllEdges = false
FEATURE [PartDesign::Body] Body  label="Spacer001"
  AllowCompound = false
  Group = -> [Sketch,Pad,Chamfer]
  Origin = -> Origin001
  Tip = -> Chamfer
FEATURE [PartDesign::CoordinateSystem] LCS_1
  AttacherType = Attacher::AttachEngine3D
  AttachmentSupport = -> [Chamfer]
  MapMode = 11
  Placement = pos=(0,0,0) rot=(0,0,1;1.5708rad)
FEATURE [App::Part] Part  label="Spacer"
  Group = -> [Body,LCS_1]
  Origin = -> Origin
---- part ../../Part/Print/Stack_Module_PSU_vent.FCStd = doc fcstd_4b052fcd0546 ----
FCSTD DOCUMENT  (FreeCAD 1.0R39319 (Git))
Label: Stack_Module_PSU_vent
License: All rights reserved
LicenseURL: https://en.wikipedia.org/wiki/All_rights_reserved
objects: Sketcher::SketchObject×26, PartDesign::Pocket×19, PartDesign::CoordinateSystem×13, PartDesign::Pad×7, PartDesign::LinearPattern×6, PartDesign::Fillet×6, PartDesign::MultiTransform×2, PartDesign::Mirrored×1, PartDesign::Body×1, App::Part×1
note: 180 computed .brp shape members not serialized (recipe doc carries the construction recipe); baked Part::Feature solids carry a one-line shape summary decoded from their .brp

FEATURE [Sketcher::SketchObject] Sketch
  ArcFitTolerance = 1e-06
  AttachmentSupport = -> [XZ_Plane001]
  FullyConstrained = true
  MakeInternals = false
  MapMode = 5
  Placement = pos=(0,0,0) rot=(1,0,0;1.5708rad)
  sketch-geometry (9):
    g0: LineSegment StartX=0 StartY=-70 StartZ=0 EndX=74 EndY=-70 EndZ=0
    g1: LineSegment StartX=74 StartY=-70 StartZ=0 EndX=74 EndY=-53.5 EndZ=0
    g2: ArcOfCircle CenterX=66.5 CenterY=-53.5 CenterZ=0 NormalX=0 NormalY=0 NormalZ=1 AngleXU=0 Radius=7.5 StartAngle=0 EndAngle=1.5708
    g3: ArcOfCircle CenterX=66.5 CenterY=-38.5 CenterZ=0 NormalX=0 NormalY=0 NormalZ=1 AngleXU=0 Radius=7.5 StartAngle=3.14159 EndAngle=4.71239
    g4: LineSegment StartX=59 StartY=-38.5 StartZ=0 EndX=59 EndY=47.8031 EndZ=0
    g5: ArcOfCircle CenterX=66.5 CenterY=47.8031 CenterZ=0 NormalX=0 NormalY=0 NormalZ=1 AngleXU=0 Radius=7.5 StartAngle=1.77215 EndAngle=3.14159
    g6: ArcOfCircle CenterX=63.5 CenterY=62.5 CenterZ=0 NormalX=0 NormalY=0 NormalZ=1 AngleXU=0 Radius=7.5 StartAngle=4.91375 EndAngle=7.85398
    g7: LineSegment StartX=63.5 StartY=70 StartZ=0 EndX=0 EndY=70 EndZ=0
    g8: LineSegment StartX=0 StartY=70 StartZ=0 EndX=0 EndY=-70 EndZ=0
  constraints (26):
    c: PointOnObject(g0,g-2)
    c: Horizontal(g0)
    c: Coincident(g0,g1)
    c: Vertical(g1)
    c: Tangent(g1,g2) = -1.5708
    c: Tangent(g2,g3) = 1.5708
    c: Tangent(g3,g4) = 1.5708
    c: Tangent(g4,g5) = 1.5708
    c: Tangent(g5,g6) = 1.5708
    c: Tangent(g6,g7) = -1.5708
    c: Coincident(g7,g8)
    c: Coincident(g8,g0)
    c: Vertical(g8)
    c: Horizontal(g7)
    c: Vertical(g4)
    c: DistanceX(g0,g0) = 74
    c: Distance(g7,g0) = 140
    c: Distance(g2,g0) = 16.5
    c: Radius(g2) = 7.5
    c: Distance(g8,g4) = 59
    c: Radius(g6) = 7.5
    c: Distance(g6,g8) = 63.5
    c: Distance(g2,g8) = 66.5
    c: Distance(g-1,g0) = 70
    c: Radius(g3) = 7.5
    c: Radius(g5) = 7.5
FEATURE [PartDesign::Pad] Pad
  Direction = (0,-1,2e-16)
  Length = 40.25
  Length2 = 10
  Placement = pos=(0,0,0) rot=(1,0,0;1.5708rad)
  Profile = -> Sketch
  ReferenceAxis = -> Sketch [N_Axis]
  Refine = true
  Suppressed = false
  Type = 0
FEATURE [Sketcher::SketchObject] Sketch001
  ArcFitTolerance = 1e-06
  AttachmentSupport = -> [Pad]
  ExternalGeometry = -> [Pad]
  FullyConstrained = true
  MakeInternals = false
  MapMode = 5
  Placement = pos=(0,-40.25,0) rot=(1,0,0;1.5708rad)
  sketch-geometry (4):
    g0: LineSegment StartX=0 StartY=-70 StartZ=0 EndX=66 EndY=-70 EndZ=0
    g1: LineSegment StartX=66 StartY=-70 StartZ=0 EndX=66 EndY=-60 EndZ=0
    g2: LineSegment StartX=66 StartY=-60 StartZ=0 EndX=0 EndY=-60 EndZ=0
    g3: LineSegment StartX=0 StartY=-60 StartZ=0 EndX=0 EndY=-70 EndZ=0
  constraints (11):
    c: Coincident(g0,g1)
    c: Coincident(g1,g2)
    c: Coincident(g2,g3)
    c: Coincident(g3,g0)
    c: Horizontal(g0)
    c: Horizontal(g2)
    c: Vertical(g1)
    c: Vertical(g3)
    c: Coincident(g0,g-3)
    c: Distance(g0,g2) = 10
    c: Distance(g1,g3) = 66
FEATURE [PartDesign::Pocket] Pocket
  BaseFeature = -> Pad
  Direction = (0,1,-2e-16)
  Length = 0
  Length2 = 5
  Offset = -3
  Placement = pos=(0,0,0) rot=(1,0,0;1.5708rad)
  Profile = -> Sketch001
  ReferenceAxis = -> Sketch001 [N_Axis]
  Refine = true
  Suppressed = false
  Type = 3
  UpToFace = -> Pad [Face10]
FEATURE [Sketcher::SketchObject] Sketch002
  ArcFitTolerance = 1e-06
  AttachmentSupport = -> [Pocket]
  ExternalGeometry = -> [Pocket]
  FullyConstrained = true
  MakeInternals = false
  MapMode = 5
  Placement = pos=(0,-40.25,0) rot=(1,0,0;1.5708rad)
  sketch-geometry (4):
    g0: LineSegment StartX=0 StartY=67 StartZ=0 EndX=0 EndY=-60 EndZ=0
    g1: LineSegment StartX=0 StartY=-60 StartZ=0 EndX=56 EndY=-60 EndZ=0
    g2: LineSegment StartX=56 StartY=-60 StartZ=0 EndX=56 EndY=67 EndZ=0
    g3: LineSegment StartX=56 StartY=67 StartZ=0 EndX=0 EndY=67 EndZ=0
  constraints (12):
    c: Coincident(g0,g1)
    c: Coincident(g1,g2)
    c: Coincident(g2,g3)
    c: Coincident(g3,g0)
    c: Vertical(g0)
    c: Vertical(g2)
    c: Horizontal(g1)
    c: Horizontal(g3)
    c: PointOnObject(g0,g-2)
    c: PointOnObject(g1,g-5)
    c: Distance(g-4,g2) = 3
    c: Distance(g-3,g3) = 3
FEATURE [PartDesign::Pocket] Pocket001
  BaseFeature = -> Pocket
  Direction = (0,1,-2e-16)
  Length = 0
  Length2 = 5
  Placement = pos=(0,0,0) rot=(1,0,0;1.5708rad)
  Profile = -> Sketch002
  ReferenceAxis = -> Sketch002 [N_Axis]
  Refine = true
  Suppressed = false
  Type = 3
  UpToFace = -> Pocket [Face6]
FEATURE [Sketcher::SketchObject] Sketch003
  ArcFitTolerance = 1e-06
  AttachmentSupport = -> [Pocket001]
  FullyConstrained = true
  MakeInternals = false
  MapMode = 5
  Placement = pos=(0,-3,0) rot=(1,0,0;1.5708rad)
  sketch-geometry (28):
    g0: LineSegment StartX=2 StartY=1.1547 StartZ=0 EndX=0 EndY=2.3094 EndZ=0
    g1: LineSegment StartX=0 StartY=2.3094 StartZ=0 EndX=-2 EndY=1.1547 EndZ=0
    g2: LineSegment StartX=-2 StartY=1.1547 StartZ=0 EndX=-2 EndY=-1.1547 EndZ=0
    g3: LineSegment StartX=-2 StartY=-1.1547 StartZ=0 EndX=0 EndY=-2.3094 EndZ=0
    g4: LineSegment StartX=0 StartY=-2.3094 StartZ=0 EndX=2 EndY=-1.1547 EndZ=0
    g5: LineSegment StartX=2 StartY=-1.1547 StartZ=0 EndX=2 EndY=1.1547 EndZ=0
    g6: Circle [constr] CenterX=0 CenterY=0 CenterZ=0 NormalX=0 NormalY=0 NormalZ=1 AngleXU=0 Radius=2.3094
    g7: LineSegment StartX=5.25 StartY=6.7847 StartZ=0 EndX=3.25 EndY=7.9394 EndZ=0
    g8: LineSegment StartX=3.25 StartY=7.9394 StartZ=0 EndX=1.25 EndY=6.7847 EndZ=0
    g9: LineSegment StartX=1.25 StartY=6.7847 StartZ=0 EndX=1.25 EndY=4.4753 EndZ=0
    g10: LineSegment StartX=1.25 StartY=4.4753 StartZ=0 EndX=3.25 EndY=3.3206 EndZ=0
    g11: LineSegment StartX=3.25 StartY=3.3206 StartZ=0 EndX=5.25 EndY=4.4753 EndZ=0
    g12: LineSegment StartX=5.25 StartY=4.4753 StartZ=0 EndX=5.25 EndY=6.7847 EndZ=0
    g13: Circle [constr] CenterX=3.25 CenterY=5.63 CenterZ=0 NormalX=0 NormalY=0 NormalZ=1 AngleXU=0 Radius=2.3094
    g14: LineSegment StartX=6.5 StartY=2.3094 StartZ=0 EndX=4.5 EndY=1.1547 EndZ=0
    g15: LineSegment StartX=4.5 StartY=1.1547 StartZ=0 EndX=4.5 EndY=-1.1547 EndZ=0
    g16: LineSegment StartX=4.5 StartY=-1.1547 StartZ=0 EndX=6.5 EndY=-2.3094 EndZ=0
    g17: LineSegment StartX=6.5 StartY=-2.3094 StartZ=0 EndX=8.5 EndY=-1.1547 EndZ=0
    g18: LineSegment StartX=8.5 StartY=-1.1547 StartZ=0 EndX=8.5 EndY=1.1547 EndZ=0
    g19: LineSegment StartX=8.5 StartY=1.1547 StartZ=0 EndX=6.5 EndY=2.3094 EndZ=0
    g20: Circle [constr] CenterX=6.5 CenterY=0 CenterZ=0 NormalX=0 NormalY=0 NormalZ=1 AngleXU=0 Radius=2.3094
    g21: LineSegment StartX=11.75 StartY=6.7847 StartZ=0 EndX=9.75 EndY=7.9394 EndZ=0
    g22: LineSegment StartX=9.75 StartY=7.9394 StartZ=0 EndX=7.75 EndY=6.7847 EndZ=0
    g23: LineSegment StartX=7.75 StartY=6.7847 StartZ=0 EndX=7.75 EndY=4.4753 EndZ=0
    g24: LineSegment StartX=7.75 StartY=4.4753 StartZ=0 EndX=9.75 EndY=3.3206 EndZ=0
    g25: LineSegment StartX=9.75 StartY=3.3206 StartZ=0 EndX=11.75 EndY=4.4753 EndZ=0
    g26: LineSegment StartX=11.75 StartY=4.4753 StartZ=0 EndX=11.75 EndY=6.7847 EndZ=0
    g27: Circle [constr] CenterX=9.75 CenterY=5.63 CenterZ=0 NormalX=0 NormalY=0 NormalZ=1 AngleXU=0 Radius=2.3094
  constraints (70):
    c: Coincident(g0,g1)
    c: Coincident(g1,g2)
    c: Coincident(g2,g3)
    c: Coincident(g3,g4)
    c: Coincident(g4,g5)
    c: Coincident(g5,g0)
    c: Equal(g0, g1-g5) x5
    c: PointOnObject(g0,g6)
    c: PointOnObject(g1,g6)
    c: PointOnObject(g2,g6)
    c: PointOnObject(g3,g6)
    c: PointOnObject(g4,g6)
    c: PointOnObject(g5,g6)
    c: Coincident(g6,g-1)
    c: PointOnObject(g0,g-2)
    c: Distance(g5,g2) = 4
    c: Coincident(g7,g8)
    c: Coincident(g8,g9)
    c: Coincident(g9,g10)
    c: Coincident(g10,g11)
    c: Coincident(g11,g12)
    c: Coincident(g12,g7)
    c: Equal(g7, g8-g12) x5
    c: PointOnObject(g7,g13)
    c: PointOnObject(g8,g13)
    c: PointOnObject(g9,g13)
    c: PointOnObject(g10,g13)
    c: PointOnObject(g11,g13)
    c: PointOnObject(g12,g13)
    c: Distance(g13,g-2) = 3.25
    c: DistanceY(g6,g13) = 5.63
    c: Vertical(g9)
    c: Coincident(g14,g15)
    c: Coincident(g15,g16)
    c: Coincident(g16,g17)
    c: Coincident(g17,g18)
    c: Coincident(g18,g19)
    c: Coincident(g19,g14)
    c: Equal(g14, g15-g19) x5
    c: PointOnObject(g14,g20)
    c: PointOnObject(g15,g20)
    c: PointOnObject(g16,g20)
    c: PointOnObject(g17,g20)
    c: PointOnObject(g18,g20)
    c: PointOnObject(g19,g20)
    c: PointOnObject(g20,g-1)
    c: Distance(g20,g-2) = 6.5
    c: Vertical(g15)
    c: Distance(g15,g5) = 2.5
    c: Distance(g10,g0) = 2.50072
    c: Distance(g5,g2) = 4
    c: Distance(g18,g15) = 4
    c: Distance(g12,g9) = 4
    c: Coincident(g21,g22)
    c: Coincident(g22,g23)
    c: Coincident(g23,g24)
    c: Coincident(g24,g25)
    c: Coincident(g25,g26)
    c: Coincident(g26,g21)
    c: Equal(g21, g22-g26) x5
    c: PointOnObject(g21,g27)
    c: PointOnObject(g22,g27)
    c: PointOnObject(g23,g27)
    c: PointOnObject(g24,g27)
    c: PointOnObject(g25,g27)
    c: PointOnObject(g26,g27)
    c: Vertical(g23)
    c: Distance(g26,g23) = 4
    c: Distance(g27,g-1) = 5.63
    c: DistanceX(g13,g27) = 6.5
FEATURE [PartDesign::Pocket] Pocket002
  BaseFeature = -> Pocket001
  Direction = (0,1,-2e-16)
  Length = 5
  Length2 = 5
  Placement = pos=(0,0,0) rot=(1,0,0;1.5708rad)
  Profile = -> Sketch003
  ReferenceAxis = -> Sketch003 [N_Axis]
  Refine = true
  Suppressed = false
  Type = 1
FEATURE [PartDesign::LinearPattern] LinearPattern
  Direction = -> X_Axis001
  Length = 39
  Mode = 1
  Occurrences = 4
  Offset = 13
  Placement = pos=(0,0,0) rot=(1,0,0;1.5708rad)
  Refine = true
  Suppressed = false
  TransformMode = 0
FEATURE [PartDesign::LinearPattern] LinearPattern001
  Direction = -> Z_Axis001
  Length = 45.04
  Mode = 1
  Occurrences = 5
  Offset = 11.26
  Placement = pos=(0,0,0) rot=(1,0,0;1.5708rad)
  Refine = true
  Reversed = true
  Suppressed = false
  TransformMode = 0
FEATURE [PartDesign::LinearPattern] LinearPattern002
  Direction = -> Z_Axis001
  Length = 11.26
  Mode = 1
  Occurrences = 2
  Offset = 11.26
  Placement = pos=(0,0,0) rot=(1,0,0;1.5708rad)
  Refine = true
  Suppressed = false
  TransformMode = 0
FEATURE [PartDesign::MultiTransform] MultiTransform
  BaseFeature = -> Pocket002
  Originals = -> [Pocket002]
  Placement = pos=(0,0,0) rot=(1,0,0;1.5708rad)
  Refine = true
  Suppressed = false
  TransformMode = 0
  Transformations = -> [LinearPattern,LinearPattern001,LinearPattern002]
FEATURE [Sketcher::SketchObject] Sketch004
  ArcFitTolerance = 1e-06
  AttachmentSupport = -> [MultiTransform]
  ExternalGeometry = -> [MultiTransform]
  FullyConstrained = true
  MakeInternals = false
  MapMode = 5
  Placement = pos=(0,-40.25,0) rot=(1,0,0;1.5708rad)
  sketch-geometry (11):
    g0: LineSegment StartX=56 StartY=-45 StartZ=0 EndX=50 EndY=-45 EndZ=0
    g1: ArcOfCircle CenterX=50 CenterY=-51 CenterZ=0 NormalX=0 NormalY=0 NormalZ=1 AngleXU=0 Radius=6 StartAngle=1.5708 EndAngle=4.71239
    g2: LineSegment StartX=50 StartY=-57 StartZ=0 EndX=56 EndY=-57 EndZ=0
    g3: LineSegment StartX=56 StartY=-57 StartZ=0 EndX=56 EndY=-45 EndZ=0
    g4: LineSegment StartX=56 StartY=22 StartZ=0 EndX=50 EndY=22 EndZ=0
    g5: ArcOfCircle CenterX=50 CenterY=16 CenterZ=0 NormalX=0 NormalY=0 NormalZ=1 AngleXU=0 Radius=6 StartAngle=1.5708 EndAngle=4.71239
    g6: LineSegment StartX=50 StartY=10 StartZ=0 EndX=56 EndY=10 EndZ=0
    g7: LineSegment StartX=56 StartY=10 StartZ=0 EndX=56 EndY=22 EndZ=0
    g8: LineSegment [constr] StartX=50 StartY=16 StartZ=0 EndX=50 EndY=-51 EndZ=0
    g9: Circle CenterX=50 CenterY=16 CenterZ=0 NormalX=0 NormalY=0 NormalZ=1 AngleXU=0 Radius=2.35
    g10: Circle CenterX=50 CenterY=-51 CenterZ=0 NormalX=0 NormalY=0 NormalZ=1 AngleXU=0 Radius=2.35
  constraints (28):
    c: Horizontal(g0)
    c: Tangent(g0,g1) = -1.5708
    c: Tangent(g1,g2) = -1.5708
    c: Coincident(g2,g3)
    c: Coincident(g3,g0)
    c: Vertical(g3)
    c: Horizontal(g2)
    c: Horizontal(g4)
    c: Tangent(g4,g5) = -1.5708
    c: Tangent(g5,g6) = -1.5708
    c: Coincident(g6,g7)
    c: Coincident(g7,g4)
    c: Vertical(g7)
    c: Horizontal(g6)
    c: Coincident(g8,g5)
    c: Coincident(g8,g1)
    c: Vertical(g8)
    c: PointOnObject(g4,g-3)
    c: PointOnObject(g0,g-3)
    c: Distance(g6,g4) = 12
    c: Distance(g2,g0) = 12
    c: Distance(g2,g-4) = 13
    c: DistanceY(g8,g8) = 67
    c: Distance(g-2,g8) = 50
    c: Coincident(g9,g5)
    c: Coincident(g10,g1)
    c: Diameter(g10) = 4.7
    c: Diameter(g9) = 4.7
FEATURE [PartDesign::Pad] Pad001
  BaseFeature = -> MultiTransform
  Direction = (0,-1,2e-16)
  Length = 5.5
  Length2 = 10
  Placement = pos=(0,0,0) rot=(1,0,0;1.5708rad)
  Profile = -> Sketch004
  ReferenceAxis = -> Sketch004 [N_Axis]
  Refine = true
  Reversed = true
  Suppressed = false
  Type = 0
FEATURE [Sketcher::SketchObject] Sketch006
  ArcFitTolerance = 1e-06
  AttachmentSupport = -> [Pad001]
  ExternalGeometry = -> [Pad001]
  FullyConstrained = true
  MakeInternals = false
  MapMode = 5
  Placement = pos=(0,-3.08e-14,-70) rot=(1,0,0;3.14159rad)
  sketch-geometry (3):
    g0: LineSegment StartX=44 StartY=37.25 StartZ=0 EndX=44 EndY=34.75 EndZ=0
    g1: LineSegment StartX=44 StartY=34.75 StartZ=0 EndX=45.4434 EndY=34.75 EndZ=0
    g2: LineSegment StartX=45.4434 StartY=34.75 StartZ=0 EndX=44 EndY=37.25 EndZ=0
  constraints (9):
    c: Vertical(g0)
    c: Coincident(g0,g1)
    c: Horizontal(g1)
    c: Coincident(g1,g2)
    c: Coincident(g2,g0)
    c: Distance(g0,g-4) = 3
    c: Distance(g-3,g0) = 12
    c: PointOnObject(g1,g-5)
    c: Angle(g0,g2) = 0.523599
FEATURE [PartDesign::Pocket] Pocket003
  BaseFeature = -> Pad001
  Direction = (0,0,1)
  Length = 0
  Length2 = 5
  Placement = pos=(0,0,0) rot=(1,0,0;1.5708rad)
  Profile = -> Sketch006
  ReferenceAxis = -> Sketch006 [N_Axis]
  Refine = true
  Suppressed = false
  Type = 3
  UpToFace = -> Pad001 [Face585]
FEATURE [Sketcher::SketchObject] Sketch007
  ArcFitTolerance = 1e-06
  AttachmentSupport = -> [Pocket003]
  ExternalGeometry = -> [Pocket003]
  FullyConstrained = true
  MakeInternals = false
  MapMode = 5
  Placement = pos=(0,-40.25,0) rot=(1,0,0;1.5708rad)
  sketch-geometry (4):
    g0: LineSegment StartX=66 StartY=-60 StartZ=0 EndX=66 EndY=-67 EndZ=0
    g1: LineSegment StartX=66 StartY=-67 StartZ=0 EndX=71 EndY=-67 EndZ=0
    g2: LineSegment StartX=71 StartY=-67 StartZ=0 EndX=71 EndY=-60 EndZ=0
    g3: LineSegment StartX=71 StartY=-60 StartZ=0 EndX=66 EndY=-60 EndZ=0
  constraints (11):
    c: Coincident(g0,g1)
    c: Coincident(g1,g2)
    c: Coincident(g2,g3)
    c: Coincident(g3,g0)
    c: Vertical(g0)
    c: Vertical(g2)
    c: Horizontal(g1)
    c: Horizontal(g3)
    c: Coincident(g0,g-3)
    c: Distance(g1,g3) = 7
    c: Distance(g2,g0) = 5
FEATURE [PartDesign::Pocket] Pocket004
  BaseFeature = -> Pocket003
  Direction = (0,1,-2e-16)
  Length = 3.2
  Length2 = 5
  Placement = pos=(0,0,0) rot=(1,0,0;1.5708rad)
  Profile = -> Sketch007
  ReferenceAxis = -> Sketch007 [N_Axis]
  Refine = true
  Suppressed = false
  Type = 0
FEATURE [Sketcher::SketchObject] Sketch008
  ArcFitTolerance = 1e-06
  AttachmentSupport = -> [Pocket004]
  ExternalGeometry = -> [Pocket004]
  FullyConstrained = true
  MakeInternals = false
  MapMode = 5
  Placement = pos=(0,-37.05,0) rot=(1,0,0;1.5708rad)
  sketch-geometry (1):
    g0: Circle CenterX=68 CenterY=-63.5 CenterZ=0 NormalX=0 NormalY=0 NormalZ=1 AngleXU=0 Radius=1.25
  constraints (3):
    c: Diameter(g0) = 2.5
    c: Distance(g0,g-2) = 68
    c: Distance(g0,g-3) = 3.5
FEATURE [PartDesign::Pocket] Pocket005
  BaseFeature = -> Pocket004
  Direction = (0,1,-2e-16)
  Length = 10
  Length2 = 5
  Placement = pos=(0,0,0) rot=(1,0,0;1.5708rad)
  Profile = -> Sketch008
  ReferenceAxis = -> Sketch008 [N_Axis]
  Refine = true
  Suppressed = false
  Type = 0
FEATURE [Sketcher::SketchObject] Sketch009
  ArcFitTolerance = 1e-06
  AttachmentSupport = -> [Pocket005]
  ExternalGeometry = -> [Pocket005]
  FullyConstrained = true
  MakeInternals = false
  MapMode = 5
  Placement = pos=(0,-3,0) rot=(1,0,0;1.5708rad)
  sketch-geometry (1):
    g0: Circle CenterX=60.5 CenterY=-65.5 CenterZ=0 NormalX=0 NormalY=0 NormalZ=1 AngleXU=0 Radius=1.5
  constraints (3):
    c: Diameter(g0) = 3
    c: Distance(g0,g-3) = 4.5
    c: Distance(g0,g-2) = 60.5
FEATURE [PartDesign::Pocket] Pocket006
  BaseFeature = -> Pocket005
  Direction = (0,1,-2e-16)
  Length = 5
  Length2 = 5
  Placement = pos=(0,0,0) rot=(1,0,0;1.5708rad)
  Profile = -> Sketch009
  ReferenceAxis = -> Sketch009 [N_Axis]
  Refine = true
  Suppressed = false
  Type = 1
FEATURE [Sketcher::SketchObject] Sketch010
  ArcFitTolerance = 1e-06
  AttachmentSupport = -> [Pocket006]
  ExternalGeometry = -> [Pocket006]
  FullyConstrained = true
  MakeInternals = false
  MapMode = 5
  Placement = pos=(-6.78e-14,0,-60) rot=(1,0,0;3.14159rad)
  sketch-geometry (3):
    g0: LineSegment [constr] StartX=59 StartY=34 StartZ=0 EndX=59 EndY=6 EndZ=0
    g1: Circle CenterX=59 CenterY=34 CenterZ=0 NormalX=0 NormalY=0 NormalZ=1 AngleXU=0 Radius=1.25
    g2: Circle CenterX=59 CenterY=6 CenterZ=0 NormalX=0 NormalY=0 NormalZ=1 AngleXU=0 Radius=1.25
  constraints (8):
    c: Vertical(g0)
    c: Coincident(g1,g0)
    c: Coincident(g2,g0)
    c: Distance(g0,g-3) = 31
    c: Distance(g-4,g0) = 3
    c: Distance(g0,g-3) = 3
    c: Diameter(g2) = 2.5
    c: Diameter(g1) = 2.5
FEATURE [PartDesign::Pocket] Pocket007
  BaseFeature = -> Pocket006
  Direction = (1.1e-15,0,1)
  Length = 10
  Length2 = 5
  Placement = pos=(0,0,0) rot=(1,0,0;1.5708rad)
  Profile = -> Sketch010
  ReferenceAxis = -> Sketch010 [N_Axis]
  Refine = true
  Suppressed = false
  Type = 0
FEATURE [Sketcher::SketchObject] Sketch011
  ArcFitTolerance = 1e-06
  AttachmentSupport = -> [Pocket007]
  ExternalGeometry = -> [Pocket007]
  FullyConstrained = true
  MakeInternals = false
  MapMode = 5
  Placement = pos=(0,-40.25,0) rot=(1,0,0;1.5708rad)
  sketch-geometry (2):
    g0: Circle CenterX=63.5 CenterY=62.5 CenterZ=0 NormalX=0 NormalY=0 NormalZ=1 AngleXU=0 Radius=3
    g1: Circle CenterX=66.5 CenterY=-53.5 CenterZ=0 NormalX=0 NormalY=0 NormalZ=1 AngleXU=0 Radius=3
  constraints (7):
    c: Coincident(g0,g-3)
    c: Coincident(g1,g-4)
    c: Diameter(g0) = 6
    c: Diameter(g1) = 6
    c: DistanceY(g1,g0) = 116
    c: Distance(g0,g-2) = 63.5
    c: DistanceX(g-1,g1) = 66.5
FEATURE [PartDesign::Pocket] Pocket008
  BaseFeature = -> Pocket007
  Direction = (0,1,-2e-16)
  Length = 5
  Length2 = 5
  Placement = pos=(0,0,0) rot=(1,0,0;1.5708rad)
  Profile = -> Sketch011
  ReferenceAxis = -> Sketch011 [N_Axis]
  Refine = true
  Suppressed = false
  Type = 1
FEATURE [Sketcher::SketchObject] Sketch012
  ArcFitTolerance = 1e-06
  AttachmentSupport = -> [Pocket008]
  ExternalGeometry = -> [Pocket008]
  FullyConstrained = true
  MakeInternals = false
  MapMode = 5
  Placement = pos=(0,-40.25,0) rot=(1,0,0;1.5708rad)
  sketch-geometry (2):
    g0: Circle CenterX=63.5 CenterY=62.5 CenterZ=0 NormalX=0 NormalY=0 NormalZ=1 AngleXU=0 Radius=4.5
    g1: Circle CenterX=66.5 CenterY=-53.5 CenterZ=0 NormalX=0 NormalY=0 NormalZ=1 AngleXU=0 Radius=4.5
  constraints (4):
    c: Coincident(g0,g-4)
    c: Coincident(g1,g-3)
    c: Diameter(g1) = 9
    c: Diameter(g0) = 9
FEATURE [PartDesign::Pocket] Pocket009
  BaseFeature = -> Pocket008
  Direction = (0,1,-2e-16)
  Length = 5
  Length2 = 5
  Placement = pos=(0,0,0) rot=(1,0,0;1.5708rad)
  Profile = -> Sketch012
  ReferenceAxis = -> Sketch012 [N_Axis]
  Refine = true
  Suppressed = false
  Type = 0
FEATURE [Sketcher::SketchObject] Sketch013
  ArcFitTolerance = 1e-06
  AttachmentSupport = -> [Pocket009]
  ExternalGeometry = -> [Pocket009]
  FullyConstrained = true
  MakeInternals = false
  MapMode = 5
  Placement = pos=(0,-3e-16,0) rot=(-1,0,0;1.5708rad)
  sketch-geometry (2):
    g0: Circle CenterX=63.5 CenterY=-62.5 CenterZ=0 NormalX=0 NormalY=0 NormalZ=1 AngleXU=0 Radius=6
    g1: Circle CenterX=66.5 CenterY=53.5 CenterZ=0 NormalX=0 NormalY=0 NormalZ=1 AngleXU=0 Radius=6
  constraints (4):
    c: Coincident(g0,g-4)
    c: Coincident(g1,g-3)
    c: Diameter(g1) = 12
    c: Diameter(g0) = 12
FEATURE [PartDesign::Pocket] Pocket010
  BaseFeature = -> Pocket009
  Direction = (0,-1,-2e-16)
  Length = 5
  Length2 = 5
  Placement = pos=(0,0,0) rot=(1,0,0;1.5708rad)
  Profile = -> Sketch013
  ReferenceAxis = -> Sketch013 [N_Axis]
  Refine = true
  Suppressed = false
  Type = 0
FEATURE [Sketcher::SketchObject] Sketch014
  ArcFitTolerance = 1e-06
  AttachmentSupport = -> [Pocket010]
  ExternalGeometry = -> [Pocket010]
  FullyConstrained = true
  MakeInternals = false
  MapMode = 5
  Placement = pos=(0,-5,0) rot=(-1,0,0;1.5708rad)
  sketch-geometry (14):
    g0: LineSegment StartX=66.5 StartY=58.25 StartZ=0 EndX=62.3864 EndY=55.875 EndZ=0
    g1: LineSegment StartX=62.3864 StartY=55.875 StartZ=0 EndX=62.3864 EndY=51.125 EndZ=0
    g2: LineSegment StartX=62.3864 StartY=51.125 StartZ=0 EndX=66.5 EndY=48.75 EndZ=0
    g3: LineSegment StartX=66.5 StartY=48.75 StartZ=0 EndX=70.6136 EndY=51.125 EndZ=0
    g4: LineSegment StartX=70.6136 StartY=51.125 StartZ=0 EndX=70.6136 EndY=55.875 EndZ=0
    g5: LineSegment StartX=70.6136 StartY=55.875 StartZ=0 EndX=66.5 EndY=58.25 EndZ=0
    g6: Circle [constr] CenterX=66.5 CenterY=53.5 CenterZ=0 NormalX=0 NormalY=0 NormalZ=1 AngleXU=0 Radius=4.75
    g7: LineSegment StartX=67.6136 StartY=-60.125 StartZ=0 EndX=63.5 EndY=-57.75 EndZ=0
    g8: LineSegment StartX=63.5 StartY=-57.75 StartZ=0 EndX=59.3864 EndY=-60.125 EndZ=0
    g9: LineSegment StartX=59.3864 StartY=-60.125 StartZ=0 EndX=59.3864 EndY=-64.875 EndZ=0
    g10: LineSegment StartX=59.3864 StartY=-64.875 StartZ=0 EndX=63.5 EndY=-67.25 EndZ=0
    g11: LineSegment StartX=63.5 StartY=-67.25 StartZ=0 EndX=67.6136 EndY=-64.875 EndZ=0
    g12: LineSegment StartX=67.6136 StartY=-64.875 StartZ=0 EndX=67.6136 EndY=-60.125 EndZ=0
    g13: Circle [constr] CenterX=63.5 CenterY=-62.5 CenterZ=0 NormalX=0 NormalY=0 NormalZ=1 AngleXU=0 Radius=4.75
  constraints (32):
    c: Coincident(g0,g1)
    c: Coincident(g1,g2)
    c: Coincident(g2,g3)
    c: Coincident(g3,g4)
    c: Coincident(g4,g5)
    c: Coincident(g5,g0)
    c: Equal(g0, g1-g5) x5
    c: PointOnObject(g0,g6)
    c: PointOnObject(g1,g6)
    c: PointOnObject(g2,g6)
    c: PointOnObject(g3,g6)
    c: PointOnObject(g4,g6)
    c: PointOnObject(g5,g6)
    c: Coincident(g7,g8)
    c: Coincident(g8,g9)
    c: Coincident(g9,g10)
    c: Coincident(g10,g11)
    c: Coincident(g11,g12)
    c: Coincident(g12,g7)
    c: Equal(g7, g8-g12) x5
    c: PointOnObject(g7,g13)
    c: PointOnObject(g8,g13)
    c: PointOnObject(g9,g13)
    c: PointOnObject(g10,g13)
    c: PointOnObject(g11,g13)
    c: PointOnObject(g12,g13)
    c: Coincident(g13,g-4)
    c: Diameter(g13) = 9.5
    c: Diameter(g6) = 9.5
    c: Coincident(g-3,g6)
    c: Vertical(g1)
    c: Vertical(g9)
FEATURE [PartDesign::Pocket] Pocket011
  BaseFeature = -> Pocket010
  Direction = (0,-1,-2e-16)
  Length = 5
  Length2 = 5
  Placement = pos=(0,0,0) rot=(1,0,0;1.5708rad)
  Profile = -> Sketch014
  ReferenceAxis = -> Sketch014 [N_Axis]
  Refine = true
  Suppressed = false
  Type = 0
FEATURE [PartDesign::Fillet] Fillet
  Base = -> Pocket011 [Edge2]
  BaseFeature = -> Pocket011
  Placement = pos=(0,0,0) rot=(1,0,0;1.5708rad)
  Radius = 3
  Refine = true
  SupportTransform = false
  Suppressed = false
  UseAllEdges = false
FEATURE [Sketcher::SketchObject] Sketch015
  ArcFitTolerance = 1e-06
  AttachmentSupport = -> [Fillet]
  ExternalGeometry = -> [Fillet]
  FullyConstrained = true
  MakeInternals = false
  MapMode = 5
  Placement = pos=(0,-3.08e-14,-70) rot=(1,0,0;3.14159rad)
  sketch-geometry (6):
    g0: LineSegment StartX=2.5 StartY=3 StartZ=0 EndX=2.5 EndY=8 EndZ=0
    g1: LineSegment StartX=2.5 StartY=8 StartZ=0 EndX=0 EndY=8 EndZ=0
    g2: LineSegment StartX=0 StartY=8 StartZ=0 EndX=0 EndY=11 EndZ=0
    g3: LineSegment StartX=0 StartY=11 StartZ=0 EndX=5.5 EndY=11 EndZ=0
    g4: LineSegment StartX=5.5 StartY=11 StartZ=0 EndX=5.5 EndY=3 EndZ=0
    g5: LineSegment StartX=5.5 StartY=3 StartZ=0 EndX=2.5 EndY=3 EndZ=0
  constraints (18):
    c: PointOnObject(g0,g-3)
    c: Vertical(g0)
    c: Coincident(g0,g1)
    c: PointOnObject(g1,g-2)
    c: Horizontal(g1)
    c: Coincident(g1,g2)
    c: PointOnObject(g2,g-2)
    c: Coincident(g2,g3)
    c: Horizontal(g3)
    c: Coincident(g3,g4)
    c: PointOnObject(g4,g-3)
    c: Vertical(g4)
    c: Coincident(g4,g5)
    c: Coincident(g5,g0)
    c: Distance(g1,g3) = 3
    c: Distance(g-2,g0) = 2.5
    c: Distance(g4,g0) = 3
    c: Distance(g1,g-3) = 5
FEATURE [PartDesign::Pad] Pad002
  BaseFeature = -> Fillet
  Direction = (0,0,-1)
  Length = 3
  Length2 = 10
  Placement = pos=(0,0,0) rot=(1,0,0;1.5708rad)
  Profile = -> Sketch015
  ReferenceAxis = -> Sketch015 [N_Axis]
  Refine = true
  Reversed = true
  Suppressed = false
  Type = 0
FEATURE [PartDesign::Fillet] Fillet001
  Base = -> Pad002 [Edge1804,Edge624]
  BaseFeature = -> Pad002
  Placement = pos=(0,0,0) rot=(1,0,0;1.5708rad)
  Radius = 3
  Refine = true
  SupportTransform = false
  Suppressed = false
  UseAllEdges = false
FEATURE [PartDesign::Mirrored] Mirrored
  BaseFeature = -> Fillet001
  MirrorPlane = -> YZ_Plane001
  Placement = pos=(0,0,0) rot=(1,0,0;1.5708rad)
  Refine = true
  Suppressed = false
  TransformMode = 1
FEATURE [Sketcher::SketchObject] Sketch016
  ArcFitTolerance = 1e-06
  AttachmentSupport = -> [Mirrored]
  ExternalGeometry = -> [Mirrored]
  FullyConstrained = true
  MakeInternals = false
  MapMode = 5
  Placement = pos=(0,5.5e-15,0) rot=(-1,0,0;1.5708rad)
  sketch-geometry (11):
    g0: Circle CenterX=-3 CenterY=30.5 CenterZ=0 NormalX=0 NormalY=0 NormalZ=1 AngleXU=0 Radius=6
    g1: Circle CenterX=-3 CenterY=-24.5 CenterZ=0 NormalX=0 NormalY=0 NormalZ=1 AngleXU=0 Radius=6
    g2: LineSegment [constr] StartX=-42 StartY=52 StartZ=0 EndX=-42 EndY=-40.5 EndZ=0
    g3: LineSegment [constr] StartX=-42 StartY=-40.5 StartZ=0 EndX=43 EndY=-40.5 EndZ=0
    g4: LineSegment [constr] StartX=43 StartY=-40.5 StartZ=0 EndX=43 EndY=52 EndZ=0
    g5: LineSegment [constr] StartX=43 StartY=52 StartZ=0 EndX=-42 EndY=52 EndZ=0
    g6: Circle CenterX=-42 CenterY=52 CenterZ=0 NormalX=0 NormalY=0 NormalZ=1 AngleXU=0 Radius=4
    g7: Circle CenterX=43 CenterY=52 CenterZ=0 NormalX=0 NormalY=0 NormalZ=1 AngleXU=0 Radius=4
    g8: Circle CenterX=43 CenterY=-40.5 CenterZ=0 NormalX=0 NormalY=0 NormalZ=1 AngleXU=0 Radius=4
    g9: Circle CenterX=-42 CenterY=-40.5 CenterZ=0 NormalX=0 NormalY=0 NormalZ=1 AngleXU=0 Radius=4
    g10: LineSegment [constr] StartX=-3 StartY=30.5 StartZ=0 EndX=-3 EndY=-24.5 EndZ=0
  constraints (28):
    c: Coincident(g2,g3)
    c: Coincident(g3,g4)
    c: Coincident(g4,g5)
    c: Coincident(g5,g2)
    c: Vertical(g2)
    c: Vertical(g4)
    c: Horizontal(g3)
    c: Horizontal(g5)
    c: Coincident(g6,g2)
    c: Coincident(g7,g4)
    c: Coincident(g8,g3)
    c: Coincident(g9,g2)
    c: Coincident(g10,g0)
    c: Coincident(g10,g1)
    c: Vertical(g10)
    c: Diameter(g6) = 8
    c: Diameter(g7) = 8
    c: Diameter(g9) = 8
    c: Diameter(g8) = 8
    c: Diameter(g0) = 12
    c: Diameter(g1) = 12
    c: Distance(g10,g-2) = 3
    c: Distance(g3,g5) = 92.5
    c: Distance(g4,g2) = 85
    c: Distance(g2,g10) = 39
    c: DistanceY(g1,g0) = 55
    c: Distance(g1,g3) = 16
    c: Distance(g5,g-3) = 8
FEATURE [PartDesign::Pad] Pad003
  BaseFeature = -> Mirrored
  Direction = (0,1,2e-16)
  Length = 10
  Length2 = 10
  Offset = 1
  Placement = pos=(0,0,0) rot=(1,0,0;1.5708rad)
  Profile = -> Sketch016
  ReferenceAxis = -> Sketch016 [N_Axis]
  Refine = true
  Reversed = true
  Suppressed = false
  Type = 3
  UpToFace = -> Mirrored [Face25]
FEATURE [Sketcher::SketchObject] Sketch017
  ArcFitTolerance = 1e-06
  AttachmentSupport = -> [Pad003]
  ExternalGeometry = -> [Pad003]
  FullyConstrained = true
  MakeInternals = false
  MapMode = 5
  Placement = pos=(0,-4,0) rot=(1,0,0;1.5708rad)
  sketch-geometry (2):
    g0: Circle CenterX=-3 CenterY=24.5 CenterZ=0 NormalX=0 NormalY=0 NormalZ=1 AngleXU=0 Radius=1.75
    g1: Circle CenterX=-3 CenterY=-30.5 CenterZ=0 NormalX=0 NormalY=0 NormalZ=1 AngleXU=0 Radius=1.75
  constraints (4):
    c: Coincident(g0,g-3)
    c: Coincident(g1,g-4)
    c: Diameter(g0) = 3.5
    c: Diameter(g1) = 3.5
FEATURE [PartDesign::Pocket] Pocket012
  BaseFeature = -> Pad003
  Direction = (0,1,-2e-16)
  Length = 5
  Length2 = 5
  Placement = pos=(0,0,0) rot=(1,0,0;1.5708rad)
  Profile = -> Sketch017
  ReferenceAxis = -> Sketch017 [N_Axis]
  Refine = true
  Suppressed = false
  Type = 1
FEATURE [Sketcher::SketchObject] Sketch018
  ArcFitTolerance = 1e-06
  AttachmentSupport = -> [Pocket012]
  ExternalGeometry = -> [Pocket012]
  FullyConstrained = true
  MakeInternals = false
  MapMode = 5
  Placement = pos=(0,-4,0) rot=(1,0,0;1.5708rad)
  sketch-geometry (2):
    g0: Circle CenterX=43 CenterY=40.5 CenterZ=0 NormalX=0 NormalY=0 NormalZ=1 AngleXU=0 Radius=1.25
    g1: Circle CenterX=-42 CenterY=-52 CenterZ=0 NormalX=0 NormalY=0 NormalZ=1 AngleXU=0 Radius=1.25
  constraints (4):
    c: Coincident(g0,g-3)
    c: Coincident(g1,g-4)
    c: Diameter(g1) = 2.5
    c: Diameter(g0) = 2.5
FEATURE [Sketcher::SketchObject] Sketch019
  ArcFitTolerance = 1e-06
  AttachmentSupport = -> [Pocket012]
  ExternalGeometry = -> [Pocket012]
  FullyConstrained = true
  MakeInternals = false
  MapMode = 5
  Placement = pos=(0,-3,0) rot=(1,0,0;1.5708rad)
  sketch-geometry (6):
    g0: LineSegment StartX=9 StartY=67 StartZ=0 EndX=9 EndY=42 EndZ=0
    g1: LineSegment StartX=9 StartY=42 StartZ=0 EndX=56 EndY=42 EndZ=0
    g2: LineSegment StartX=56 StartY=42 StartZ=0 EndX=56 EndY=39 EndZ=0
    g3: LineSegment StartX=56 StartY=39 StartZ=0 EndX=6 EndY=39 EndZ=0
    g4: LineSegment StartX=6 StartY=39 StartZ=0 EndX=6 EndY=67 EndZ=0
    g5: LineSegment StartX=6 StartY=67 StartZ=0 EndX=9 EndY=67 EndZ=0
  constraints (18):
    c: PointOnObject(g0,g-3)
    c: Vertical(g0)
    c: Coincident(g0,g1)
    c: PointOnObject(g1,g-4)
    c: Horizontal(g1)
    c: Coincident(g1,g2)
    c: PointOnObject(g2,g-4)
    c: Coincident(g2,g3)
    c: Horizontal(g3)
    c: Coincident(g3,g4)
    c: PointOnObject(g4,g-3)
    c: Vertical(g4)
    c: Coincident(g4,g5)
    c: Coincident(g5,g0)
    c: Distance(g4,g0) = 3
    c: Distance(g1,g3) = 3
    c: Distance(g-5,g1) = 1.5
    c: Distance(g-4,g0) = 47
FEATURE [PartDesign::Pad] Pad004
  BaseFeature = -> Pocket012
  Direction = (0,-1,2e-16)
  Length = 1
  Length2 = 10
  Placement = pos=(0,0,0) rot=(1,0,0;1.5708rad)
  Profile = -> Sketch019
  ReferenceAxis = -> Sketch019 [N_Axis]
  Refine = true
  Suppressed = false
  Type = 0
FEATURE [PartDesign::Pocket] Pocket013
  BaseFeature = -> Pad004
  Direction = (0,1,-2e-16)
  Length = 3
  Length2 = 5
  Placement = pos=(0,0,0) rot=(1,0,0;1.5708rad)
  Profile = -> Sketch018
  ReferenceAxis = -> Sketch018 [N_Axis]
  Refine = true
  Suppressed = false
  Type = 0
FEATURE [Sketcher::SketchObject] Sketch020
  ArcFitTolerance = 1e-06
  AttachmentSupport = -> [Pocket013]
  ExternalGeometry = -> [Pocket013]
  FullyConstrained = true
  MakeInternals = false
  MapMode = 5
  Placement = pos=(0,-3,0) rot=(1,0,0;1.5708rad)
  sketch-geometry (16):
    g0: LineSegment StartX=-56 StartY=67 StartZ=0 EndX=-56 EndY=59 EndZ=0
    g1: LineSegment StartX=-56 StartY=59 StartZ=0 EndX=-46 EndY=59 EndZ=0
    g2: LineSegment StartX=-46 StartY=59 StartZ=0 EndX=-46 EndY=67 EndZ=0
    g3: LineSegment StartX=-46 StartY=67 StartZ=0 EndX=-56 EndY=67 EndZ=0
    g4: LineSegment StartX=-2 StartY=59 StartZ=0 EndX=6 EndY=59 EndZ=0
    g5: LineSegment StartX=6 StartY=59 StartZ=0 EndX=6 EndY=67 EndZ=0
    g6: LineSegment StartX=6 StartY=67 StartZ=0 EndX=-2 EndY=67 EndZ=0
    g7: LineSegment StartX=9 StartY=67 StartZ=0 EndX=17 EndY=67 EndZ=0
    g8: LineSegment StartX=17 StartY=67 StartZ=0 EndX=17 EndY=59 EndZ=0
    g9: LineSegment StartX=17 StartY=59 StartZ=0 EndX=9 EndY=59 EndZ=0
    g10: LineSegment StartX=9 StartY=59 StartZ=0 EndX=9 EndY=67 EndZ=0
    g11: LineSegment StartX=49 StartY=39 StartZ=0 EndX=49 EndY=27 EndZ=0
    g12: LineSegment StartX=49 StartY=27 StartZ=0 EndX=56 EndY=27 EndZ=0
    g13: LineSegment StartX=56 StartY=27 StartZ=0 EndX=56 EndY=39 EndZ=0
    g14: LineSegment StartX=56 StartY=39 StartZ=0 EndX=49 EndY=39 EndZ=0
    g15: LineSegment StartX=-2 StartY=67 StartZ=0 EndX=-2 EndY=59 EndZ=0
  constraints (44):
    c: PointOnObject(g0,g-4)
    c: Coincident(g0,g1)
    c: Horizontal(g1)
    c: Coincident(g1,g2)
    c: PointOnObject(g2,g-3)
    c: Vertical(g2)
    c: Coincident(g2,g3)
    c: Coincident(g3,g0)
    c: PointOnObject(g4,g-5)
    c: Horizontal(g4)
    c: Coincident(g4,g5)
    c: Coincident(g5,g-5)
    c: Coincident(g5,g6)
    c: Horizontal(g6)
    c: Coincident(g-6,g7)
    c: PointOnObject(g7,g-3)
    c: Coincident(g7,g8)
    c: Vertical(g8)
    c: Coincident(g8,g9)
    c: PointOnObject(g9,g-6)
    c: Horizontal(g9)
    c: Coincident(g9,g10)
    c: Coincident(g10,g7)
    c: PointOnObject(g11,g-8)
    c: Vertical(g11)
    c: Coincident(g11,g12)
    c: PointOnObject(g12,g-7)
    c: Horizontal(g12)
    c: Coincident(g12,g13)
    c: Coincident(g13,g-8)
    c: Coincident(g13,g14)
    c: Coincident(g14,g11)
    c: Distance(g1,g3) = 8
    c: Distance(g4,g6) = 8
    c: Distance(g9,g7) = 8
    c: Distance(g2,g0) = 10
    c: Distance(g8,g10) = 8
    c: Distance(g13,g11) = 7
    c: Distance(g12,g14) = 12
    c: Coincident(g15,g6)
    c: Coincident(g15,g4)
    c: Vertical(g15)
    c: Distance(g5,g15) = 8
    c: Coincident(g0,g-4)
FEATURE [PartDesign::Pad] Pad005
  BaseFeature = -> Pocket013
  Direction = (0,-1,2e-16)
  Length = 5
  Length2 = 10
  Placement = pos=(0,0,0) rot=(1,0,0;1.5708rad)
  Profile = -> Sketch020
  ReferenceAxis = -> Sketch020 [N_Axis]
  Refine = true
  Suppressed = false
  Type = 0
FEATURE [PartDesign::Fillet] Fillet002
  Base = -> Pad005 [Edge3552,Edge3566,Edge3712,Edge3580]
  BaseFeature = -> Pad005
  Placement = pos=(0,0,0) rot=(1,0,0;1.5708rad)
  Radius = 4
  Refine = true
  SupportTransform = false
  Suppressed = false
  UseAllEdges = false
FEATURE [Sketcher::SketchObject] Sketch021
  ArcFitTolerance = 1e-06
  AttachmentSupport = -> [Fillet002]
  ExternalGeometry = -> [Fillet002]
  FullyConstrained = true
  MakeInternals = false
  MapMode = 5
  Placement = pos=(0,-8,1.8e-15) rot=(1,0,0;1.5708rad)
  sketch-geometry (4):
    g0: Circle CenterX=-50 CenterY=63 CenterZ=0 NormalX=0 NormalY=0 NormalZ=1 AngleXU=0 Radius=1.25
    g1: Circle CenterX=2 CenterY=63 CenterZ=0 NormalX=0 NormalY=0 NormalZ=1 AngleXU=0 Radius=1.25
    g2: Circle CenterX=13 CenterY=63 CenterZ=0 NormalX=0 NormalY=0 NormalZ=1 AngleXU=0 Radius=1.25
    g3: Circle CenterX=53 CenterY=31 CenterZ=0 NormalX=0 NormalY=0 NormalZ=1 AngleXU=0 Radius=1.25
  constraints (8):
    c: Coincident(g0,g-3)
    c: Coincident(g1,g-4)
    c: Coincident(g2,g-5)
    c: Coincident(g3,g-6)
    c: Diameter(g3) = 2.5
    c: Diameter(g2) = 2.5
    c: Diameter(g1) = 2.5
    c: Diameter(g0) = 2.5
FEATURE [PartDesign::Pocket] Pocket014
  BaseFeature = -> Fillet002
  Direction = (0,1,-2e-16)
  Length = 5
  Length2 = 5
  Placement = pos=(0,0,0) rot=(1,0,0;1.5708rad)
  Profile = -> Sketch021
  ReferenceAxis = -> Sketch021 [N_Axis]
  Refine = true
  Suppressed = false
  Type = 0
FEATURE [Sketcher::SketchObject] Sketch022
  ArcFitTolerance = 1e-06
  AttachmentSupport = -> [Pocket014]
  ExternalGeometry = -> [Pocket014]
  FullyConstrained = true
  MakeInternals = false
  MapMode = 5
  Placement = pos=(0,2.45e-14,70) rot=(0,0,1;3.14159rad)
  sketch-geometry (10):
    g0: LineSegment StartX=-61.75 StartY=20.125 StartZ=0 EndX=-53 EndY=40.25 EndZ=0
    g1: LineSegment StartX=-53 StartY=40.25 StartZ=0 EndX=-25.5 EndY=40.25 EndZ=0
    g2: LineSegment StartX=-25.5 StartY=40.25 StartZ=0 EndX=-16.75 EndY=20.125 EndZ=0
    g3: LineSegment StartX=-16.75 StartY=20.125 StartZ=0 EndX=-25.5 EndY=0 EndZ=0
    g4: LineSegment StartX=-25.5 StartY=0 StartZ=0 EndX=-53 EndY=0 EndZ=0
    g5: LineSegment StartX=-53 StartY=0 StartZ=0 EndX=-61.75 EndY=20.125 EndZ=0
    g6: LineSegment [constr] StartX=-61.75 StartY=20.125 StartZ=0 EndX=-16.75 EndY=20.125 EndZ=0
    g7: LineSegment [constr] StartX=-39.25 StartY=40.25 StartZ=0 EndX=-39.25 EndY=0 EndZ=0
    g8: GeomPoint [constr] X=-39.25 Y=20.125 Z=0
    g9: GeomPoint [constr] X=-39.25 Y=20.125 Z=0
  constraints (23):
    c: Coincident(g0,g1)
    c: Horizontal(g1)
    c: Coincident(g1,g2)
    c: Coincident(g2,g3)
    c: Coincident(g3,g4)
    c: Horizontal(g4)
    c: Coincident(g4,g5)
    c: Coincident(g5,g0)
    c: Coincident(g6,g0)
    c: Coincident(g6,g2)
    c: Horizontal(g6)
    c: Symmetric(g1,g1,g7)
    c: Symmetric(g4,g4,g7)
    c: Vertical(g7)
    c: DistanceX(g6,g6) = 45
    c: PointOnObject(g7,g-3)
    c: PointOnObject(g7,g-1)
    c: Symmetric(g6,g6,g8)
    c: Symmetric(g7,g7,g9)
    c: Coincident(g8,g9)
    c: DistanceX(g1,g-1) = 25.5
    c: Distance(g1,g1) = 27.5
    c: DistanceX(g4,g4) = 27.5
FEATURE [PartDesign::Pad] Pad006  label="PowerPlug Pad"
  BaseFeature = -> Pocket014
  Direction = (0,0,1)
  Length = 20
  Length2 = 10
  Placement = pos=(0,0,0) rot=(1,0,0;1.5708rad)
  Profile = -> Sketch022
  ReferenceAxis = -> Sketch022 [N_Axis]
  Refine = true
  Suppressed = false
  Type = 0
FEATURE [PartDesign::Fillet] Fillet003
  Base = -> Pad006 [Edge3677,Edge3683]
  BaseFeature = -> Pad006
  Placement = pos=(0,0,0) rot=(1,0,0;1.5708rad)
  Radius = 4
  Refine = true
  SupportTransform = false
  Suppressed = false
  UseAllEdges = false
FEATURE [PartDesign::Fillet] Fillet004
  Base = -> Fillet003 [Edge1227,Edge1]
  BaseFeature = -> Fillet003
  Placement = pos=(0,0,0) rot=(1,0,0;1.5708rad)
  Radius = 3
  Refine = true
  SupportTransform = false
  Suppressed = false
  UseAllEdges = false
FEATURE [Sketcher::SketchObject] Sketch023
  ArcFitTolerance = 1e-06
  AttachmentSupport = -> [Fillet004]
  ExternalGeometry = -> [Fillet004]
  FullyConstrained = true
  MakeInternals = false
  MapMode = 5
  Placement = pos=(0,0,90) rot=(0,0,1;3.14159rad)
  sketch-geometry (7):
    g0: LineSegment StartX=-53.5 StartY=36.5 StartZ=0 EndX=-25 EndY=36.5 EndZ=0
    g1: LineSegment StartX=-25 StartY=36.5 StartZ=0 EndX=-25 EndY=9 EndZ=0
    g2: LineSegment StartX=-25 StartY=9 StartZ=0 EndX=-31 EndY=3 EndZ=0
    g3: LineSegment StartX=-31 StartY=3 StartZ=0 EndX=-47.5 EndY=3 EndZ=0
    g4: LineSegment StartX=-47.5 StartY=3 StartZ=0 EndX=-53.5 EndY=9 EndZ=0
    g5: LineSegment StartX=-53.5 StartY=9 StartZ=0 EndX=-53.5 EndY=36.5 EndZ=0
    g6: LineSegment [constr] StartX=-39.25 StartY=36.5 StartZ=0 EndX=-39.25 EndY=3 EndZ=0
  constraints (20):
    c: Horizontal(g0)
    c: Coincident(g0,g1)
    c: Vertical(g1)
    c: Coincident(g1,g2)
    c: Coincident(g2,g3)
    c: Horizontal(g3)
    c: Coincident(g3,g4)
    c: Coincident(g4,g5)
    c: Coincident(g5,g0)
    c: Vertical(g5)
    c: Symmetric(g0,g0,g6)
    c: Symmetric(g3,g3,g6)
    c: Vertical(g6)
    c: Distance(g1,g5) = 28.5
    c: Distance(g3,g5) = 6
    c: Distance(g4,g3) = 6
    c: Distance(g3,g0) = 33.5
    c: Distance(g1,g3) = 6
    c: PointOnObject(g6,g-4)
    c: Distance(g5,g-3) = 2.5
FEATURE [PartDesign::Pocket] Pocket015  label="PowerPlug Pocket"
  BaseFeature = -> Fillet004
  Direction = (0,0,-1)
  Length = 0
  Length2 = 5
  Placement = pos=(0,0,0) rot=(1,0,0;1.5708rad)
  Profile = -> Sketch023
  ReferenceAxis = -> Sketch023 [N_Axis]
  Refine = true
  Suppressed = false
  Type = 3
  UpToFace = -> Fillet004 [Face43]
FEATURE [PartDesign::Fillet] Fillet005
  Base = -> Pocket015 [Edge1380,Edge1385,Edge1384,Edge1383,Edge1381,Edge1382]
  BaseFeature = -> Pocket015
  Placement = pos=(0,0,0) rot=(1,0,0;1.5708rad)
  Radius = 1
  Refine = true
  SupportTransform = false
  Suppressed = false
  UseAllEdges = false
FEATURE [Sketcher::SketchObject] Sketch024
  ArcFitTolerance = 1e-06
  AttachmentSupport = -> [Fillet005]
  ExternalGeometry = -> [Fillet005]
  FullyConstrained = true
  MakeInternals = false
  MapMode = 5
  Placement = pos=(0,0,90) rot=(0,0,1;3.14159rad)
  sketch-geometry (3):
    g0: Circle CenterX=-57.3883 CenterY=20.125 CenterZ=0 NormalX=0 NormalY=0 NormalZ=1 AngleXU=0 Radius=1.1
    g1: Circle CenterX=-21.1117 CenterY=20.125 CenterZ=0 NormalX=0 NormalY=0 NormalZ=1 AngleXU=0 Radius=1.1
    g2: LineSegment [constr] StartX=-57.3883 StartY=20.125 StartZ=0 EndX=-21.1117 EndY=20.125 EndZ=0
  constraints (6):
    c: Coincident(g2,g0)
    c: Coincident(g2,g1)
    c: Coincident(g-3,g0)
    c: Coincident(g1,g-4)
    c: Diameter(g1) = 2.2
    c: Diameter(g0) = 2.2
FEATURE [PartDesign::Pocket] Pocket016  label="PowerPlug Holes"
  BaseFeature = -> Fillet005
  Direction = (0,0,-1)
  Length = 0
  Length2 = 5
  Placement = pos=(0,0,0) rot=(1,0,0;1.5708rad)
  Profile = -> Sketch024
  ReferenceAxis = -> Sketch024 [N_Axis]
  Refine = true
  Suppressed = false
  Type = 3
  UpToFace = -> Fillet005 [Face22]
FEATURE [Sketcher::SketchObject] Sketch025
  ArcFitTolerance = 1e-06
  AttachmentSupport = -> [Pocket016]
  ExternalGeometry = -> [Pocket016]
  FullyConstrained = true
  MakeInternals = false
  MapMode = 5
  Placement = pos=(0,-40.25,0) rot=(1,0,0;1.5708rad)
  sketch-geometry (8):
    g0: LineSegment StartX=56 StartY=3.69e-14 StartZ=0 EndX=59 EndY=3 EndZ=0
    g1: LineSegment StartX=59 StartY=3 StartZ=0 EndX=59 EndY=0 EndZ=0
    g2: LineSegment StartX=59 StartY=0 StartZ=0 EndX=56 EndY=-3 EndZ=0
    g3: LineSegment StartX=56 StartY=-3 StartZ=0 EndX=56 EndY=3.69e-14 EndZ=0
    g4: LineSegment StartX=-56 StartY=1.839e-12 StartZ=0 EndX=-59 EndY=3 EndZ=0
    g5: LineSegment StartX=-59 StartY=3 StartZ=0 EndX=-59 EndY=0 EndZ=0
    g6: LineSegment StartX=-59 StartY=0 StartZ=0 EndX=-56 EndY=-3 EndZ=0
    g7: LineSegment StartX=-56 StartY=-3 StartZ=0 EndX=-56 EndY=1.839e-12 EndZ=0
  constraints (24):
    c: Coincident(g0,g1)
    c: Vertical(g1)
    c: Coincident(g1,g2)
    c: Coincident(g2,g3)
    c: Coincident(g3,g0)
    c: Vertical(g3)
    c: Parallel(g2,g0)
    c: PointOnObject(g0,g-4)
    c: PointOnObject(g0,g-3)
    c: Angle(g0,g3) = 0.785398
    c: DistanceY(g1,g1) = 3
    c: PointOnObject(g1,g-1)
    c: Coincident(g5,g6)
    c: PointOnObject(g6,g-5)
    c: Coincident(g6,g7)
    c: Coincident(g7,g4)
    c: Vertical(g7)
    c: DistanceY(g5,g5) = 3
    c: Parallel(g6,g4)
    c: Coincident(g4,g5)
    c: Vertical(g5)
    c: PointOnObject(g4,g-6)
    c: PointOnObject(g5,g-1)
    c: Angle(g7,g6) = 0.785398
FEATURE [PartDesign::Pocket] Pocket017
  BaseFeature = -> Pocket016
  Direction = (0,1,-2e-16)
  Length = 31.25
  Length2 = -6
  Placement = pos=(0,0,0) rot=(1,0,0;1.5708rad)
  Profile = -> Sketch025
  ReferenceAxis = -> Sketch025 [N_Axis]
  Refine = true
  Suppressed = false
  Type = 4
FEATURE [PartDesign::LinearPattern] LinearPattern003
  Direction = -> Z_Axis001
  Length = 24
  Mode = 1
  Occurrences = 5
  Offset = 6
  Placement = pos=(0,0,0) rot=(1,0,0;1.5708rad)
  Refine = true
  Suppressed = false
  TransformMode = 0
FEATURE [PartDesign::LinearPattern] LinearPattern004
  Direction = -> Z_Axis001
  Length = 30
  Mode = 1
  Occurrences = 6
  Offset = 6
  Placement = pos=(0,0,0) rot=(1,0,0;1.5708rad)
  Refine = true
  Reversed = true
  Suppressed = false
  TransformMode = 0
FEATURE [PartDesign::MultiTransform] MultiTransform001
  BaseFeature = -> Pocket017
  Originals = -> [Pocket017]
  Placement = pos=(0,0,0) rot=(1,0,0;1.5708rad)
  Refine = true
  Suppressed = false
  TransformMode = 0
  Transformations = -> [LinearPattern003,LinearPattern004]
FEATURE [Sketcher::SketchObject] Sketch026
  ArcFitTolerance = 1e-06
  AttachmentSupport = -> [MultiTransform001]
  ExternalGeometry = -> [MultiTransform001]
  FullyConstrained = true
  MakeInternals = false
  MapMode = 5
  Placement = pos=(0,-40.25,0) rot=(1,0,0;1.5708rad)
  sketch-geometry (4):
    g0: LineSegment StartX=-53 StartY=70 StartZ=0 EndX=-56 EndY=67 EndZ=0
    g1: LineSegment StartX=-56 StartY=67 StartZ=0 EndX=-53 EndY=67 EndZ=0
    g2: LineSegment StartX=-53 StartY=67 StartZ=0 EndX=-50 EndY=70 EndZ=0
    g3: LineSegment StartX=-50 StartY=70 StartZ=0 EndX=-53 EndY=70 EndZ=0
  constraints (11):
    c: PointOnObject(g0,g-3)
    c: Coincident(g0,g1)
    c: PointOnObject(g1,g-4)
    c: Coincident(g1,g2)
    c: PointOnObject(g2,g-3)
    c: Coincident(g2,g3)
    c: Coincident(g3,g0)
    c: Angle(g1,g0) = 0.785398
    c: Distance(g3,g3) = 3
    c: Parallel(g0,g2)
    c: Coincident(g-5,g0)
FEATURE [PartDesign::Pocket] Pocket018
  BaseFeature = -> MultiTransform001
  Direction = (0,1,-2e-16)
  Length = 31.25
  Length2 = -6
  Placement = pos=(0,0,0) rot=(1,0,0;1.5708rad)
  Profile = -> Sketch026
  ReferenceAxis = -> Sketch026 [N_Axis]
  Refine = true
  Suppressed = false
  Type = 4
FEATURE [PartDesign::LinearPattern] LinearPattern005
  BaseFeature = -> Pocket018
  Direction = -> X_Axis001
  Length = 60
  Mode = 1
  Occurrences = 11
  Offset = 6
  Originals = -> [Pocket018]
  Placement = pos=(0,0,0) rot=(1,0,0;1.5708rad)
  Refine = true
  Suppressed = false
  TransformMode = 0
FEATURE [PartDesign::Body] Body  label="Stack_Module_PSU_vent001"
  AllowCompound = false
  Group = -> [Sketch,Pad,Sketch001,Pocket,Sketch002,Pocket001,Sketch003,Pocket002,MultiTransform,LinearPattern,LinearPattern001,LinearPattern002,Sketch004,Pad001,Sketch006,Pocket003,Sketch007,Pocket004,Sketch008,Pocket005,Sketch009,Pocket006,Sketch010,Pocket007,Sketch011,Pocket008,Sketch012,Pocket009,Sketch013,Pocket010,Sketch014,Pocket011,Fillet,Sketch015,Pad002,Fillet001,Mirrored,Sketch016,Pad003,Sketch017,+27 more]
  Origin = -> Origin001
  Tip = -> LinearPattern005
FEATURE [PartDesign::CoordinateSystem] LCS_1  label="foot_1"
  AttacherType = Attacher::AttachEngine3D
  AttachmentSupport = -> [LinearPattern005]
  MapMode = 11
  Placement = pos=(66.5,0,-53.5) rot=(0.57735,-0.57735,-0.57735;4.18879rad)
FEATURE [PartDesign::CoordinateSystem] LCS_2  label="foot_2"
  AttacherType = Attacher::AttachEngine3D
  AttachmentSupport = -> [LinearPattern005]
  MapMode = 11
  Placement = pos=(63.5,0,62.5) rot=(0.57735,-0.57735,-0.57735;4.18879rad)
FEATURE [PartDesign::CoordinateSystem] LCS_3  label="foot_3"
  AttacherType = Attacher::AttachEngine3D
  AttachmentSupport = -> [LinearPattern005]
  MapMode = 11
  Placement = pos=(-66.5,1.48e-14,-53.5) rot=(0.57735,0.57735,-0.57735;2.0944rad)
FEATURE [PartDesign::CoordinateSystem] LCS_4  label="foot_4"
  AttacherType = Attacher::AttachEngine3D
  AttachmentSupport = -> [LinearPattern005]
  MapMode = 11
  Placement = pos=(-63.5,1.41e-14,62.5) rot=(0.57735,0.57735,-0.57735;2.0944rad)
FEATURE [PartDesign::CoordinateSystem] upper_attachment
  AttacherType = Attacher::AttachEngine3D
  AttachmentSupport = -> [LinearPattern005]
  MapMode = 11
  Placement = pos=(-63.5,-40.25,62.5) rot=(0.57735,0.57735,0.57735;4.18879rad)
FEATURE [PartDesign::CoordinateSystem] PSU_attachment
  AttacherType = Attacher::AttachEngine3D
  AttachmentSupport = -> [LinearPattern005]
  MapMode = 11
  Placement = pos=(-3,-4,-30.5) rot=(0.57735,-0.57735,0.57735;2.0944rad)
FEATURE [PartDesign::CoordinateSystem] screen_attachment
  AttacherType = Attacher::AttachEngine3D
  AttachmentSupport = -> [LinearPattern005]
  MapMode = 11
  Placement = pos=(-60.5,-3,-65.5) rot=(0.57735,0.57735,0.57735;4.18879rad)
FEATURE [PartDesign::CoordinateSystem] powerplug_attachment
  AttacherType = Attacher::AttachEngine3D
  AttachmentSupport = -> [LinearPattern005]
  MapMode = 11
  Placement = pos=(21.1117,-20.125,90) rot=(0,0,-1;1.5708rad)
FEATURE [PartDesign::CoordinateSystem] spacer_att  label="spacer_att_1"
  AttacherType = Attacher::AttachEngine3D
  AttachmentSupport = -> [LinearPattern005]
  MapMode = 11
  Placement = pos=(66.5,-35.25,-53.5) rot=(0.57735,-0.57735,0.57735;2.0944rad)
FEATURE [PartDesign::CoordinateSystem] spacer_att_2
  AttacherType = Attacher::AttachEngine3D
  AttachmentSupport = -> [LinearPattern005]
  MapMode = 11
  Placement = pos=(63.5,-35.25,62.5) rot=(0.57735,-0.57735,0.57735;2.0944rad)
FEATURE [PartDesign::CoordinateSystem] spacer_att_3
  AttacherType = Attacher::AttachEngine3D
  AttachmentSupport = -> [LinearPattern005]
  MapMode = 11
  Placement = pos=(-63.5,-35.25,62.5) rot=(0.57735,0.57735,0.57735;4.18879rad)
FEATURE [PartDesign::CoordinateSystem] spacer_att_004
  AttacherType = Attacher::AttachEngine3D
  AttachmentSupport = -> [LinearPattern005]
  MapMode = 11
  Placement = pos=(-66.5,-35.25,-53.5) rot=(0.57735,0.57735,0.57735;4.18879rad)
FEATURE [PartDesign::CoordinateSystem] linecover_att
  AttacherType = Attacher::AttachEngine3D
  AttachmentSupport = -> [LinearPattern005]
  MapMode = 11
  Placement = pos=(13,-8,63) rot=(0.57735,-0.57735,0.57735;2.0944rad)
FEATURE [App::Part] Part  label="Stack_Module_PSU_vent"
  Group = -> [Body,LCS_1,LCS_2,LCS_3,LCS_4,upper_attachment,PSU_attachment,screen_attachment,powerplug_attachment,spacer_att,spacer_att_2,spacer_att_3,spacer_att_004,linecover_att]
  Origin = -> Origin
---- part ../../Part/Purchase/LRS-75.FCStd = doc fcstd_7594911bc808 ----
FCSTD DOCUMENT  (FreeCAD 1.0R39319 (Git))
Label: LRS-75
License: All rights reserved
LicenseURL: https://en.wikipedia.org/wiki/All_rights_reserved
objects: Part::Feature×3, PartDesign::CoordinateSystem×3, Part::Refine×3, App::Part×1
note: 9 computed .brp shape members not serialized (recipe doc carries the construction recipe); baked Part::Feature solids carry a one-line shape summary decoded from their .brp

FEATURE [Part::Feature] Part__Feature  label="TY_2"
  Placement = pos=(-30,0,0.2) rot=(0,0,1;0rad)
  shape: bbox 99.02 x 97.65 x 30.2 mm, 1471 faces (baked)
FEATURE [Part::Feature] Part__Feature001  label="TN_1_1_1_1_1"
  Placement = pos=(-299.667,159.449,37.1256) rot=(0,1,0;1.5708rad)
  shape: bbox 18 x 50.7 x 15 mm, 182 faces (baked)
FEATURE [Part::Feature] Part__Feature002  label="PCB"
  shape: bbox 92 x 94.4 x 1.6 mm, 16 faces (baked)
FEATURE [PartDesign::CoordinateSystem] stack_attach
  AttacherType = Attacher::AttachEngine3D
  AttachmentSupport = -> [Part__Feature]
  MapMode = 11
  Placement = pos=(-224.029,248.825,-6.6) rot=(0,0,1;3.14104rad)
FEATURE [PartDesign::CoordinateSystem] screw1
  AttacherType = Attacher::AttachEngine3D
  AttachmentSupport = -> [Part__Feature]
  MapMode = 11
  Placement = pos=(-295.167,294.825,-5.4) rot=(-0.706748,0.707465,0;3.14159rad)
FEATURE [PartDesign::CoordinateSystem] screw2
  AttacherType = Attacher::AttachEngine3D
  AttachmentSupport = -> [Part__Feature]
  MapMode = 11
  Placement = pos=(-202.667,209.825,-5.4) rot=(-0.086033,0.996292,0;3.14159rad)
FEATURE [App::Part] LRS_75_ASM  label="LRS-75_ASM"
  Group = -> [Part__Feature,Part__Feature001,Part__Feature002,stack_attach,screw1,screw2]
  Origin = -> Origin001
FEATURE [Part::Refine] Part__Feature003  label="TY_003"
  Source = -> Part__Feature
FEATURE [Part::Refine] Part__Feature004  label="TN_1_1_1_1_002"
  Source = -> Part__Feature001
FEATURE [Part::Refine] Part__Feature005  label="PCB001"
  Source = -> Part__Feature002
---- part Assy_Foot.FCStd = doc fcstd_42735f839a23 ----
FCSTD DOCUMENT  (FreeCAD 1.0R39319 (Git))
Label: Assy_Foot
License: All rights reserved
LicenseURL: https://en.wikipedia.org/wiki/All_rights_reserved
objects: App::DocumentObjectGroup×3, PartDesign::CoordinateSystem×1, App::FeaturePython×1, App::Link×1, Part::FeaturePython×1, App::Part×1
note: 2 computed .brp shape members not serialized (recipe doc carries the construction recipe); baked Part::Feature solids carry a one-line shape summary decoded from their .brp
EXTERNAL_REF file=../../Part/Print/Foot.FCStd obj=base
EXTERNAL_REF file=../../Part/Print/Foot.FCStd obj=Part

FEATURE [App::DocumentObjectGroup] Parts
FEATURE [PartDesign::CoordinateSystem] LCS_Origin
  AttacherType = Attacher::AttachEngine3D
  AttachmentSupport = -> [X_Axis]
  MapMode = 2
FEATURE [App::DocumentObjectGroup] Constraints
FEATURE [App::FeaturePython] Variables  # WARN: FeaturePython — macro-defined, semantics opaque (R4)
  Type = App::PropertyContainer
FEATURE [App::DocumentObjectGroup] Configurations
FEATURE [App::Link] Foot
  AttachedBy = #base
  AttachedTo = Parent Assembly#LCS_Origin
  LinkPlacement = pos=(2e-15,0,0) rot=(0,0,1;1.5708rad)
  LinkedObject = -> <external ../../Part/Print/Foot.FCStd>#Part
  Placement = pos=(2e-15,0,0) rot=(0,0,1;1.5708rad)
  SolverId = Asm4EE
  expr: Placement = LCS_Origin.Placement * AttachmentOffset * Foot#base.Placement ^ -1
FEATURE [Part::FeaturePython] Nut  label="M5-Nut"  # WARN: FeaturePython — macro-defined, semantics opaque (R4)
  BaseObject = -> Foot [Body.Chamfer.Edge29]
  Diameter = 1
  Invert = false
  LeftHanded = false
  MatchOuter = false
  OffsetAngle = 0
  Placement = pos=(0,0,4) rot=(0,0,1;0rad)
  Thread = false
  Type = 33
FEATURE [App::Part] Assembly  label="Assy_Foot"
  AssemblyType = Part::Link
  Group = -> [LCS_Origin,Constraints,Variables,Configurations,Foot,Nut]
  Origin = -> Origin
  Type = Assembly
---- part Assy_M5_rod.FCStd = doc fcstd_230cf2ffa1fd ----
FCSTD DOCUMENT  (FreeCAD 1.0R39319 (Git))
Label: Assy_M5_rod
License: All rights reserved
LicenseURL: https://en.wikipedia.org/wiki/All_rights_reserved
objects: App::DocumentObjectGroup×3, PartDesign::CoordinateSystem×1, App::FeaturePython×1, App::Link×1, Part::FeaturePython×1, App::Part×1
note: 2 computed .brp shape members not serialized (recipe doc carries the construction recipe); baked Part::Feature solids carry a one-line shape summary decoded from their .brp
EXTERNAL_REF file=../../Part/Purchase/M5_rod.FCStd obj=bottom
EXTERNAL_REF file=../../Part/Purchase/M5_rod.FCStd obj=Part

FEATURE [App::DocumentObjectGroup] Parts
FEATURE [PartDesign::CoordinateSystem] LCS_Origin
  AttacherType = Attacher::AttachEngine3D
  AttachmentSupport = -> [X_Axis]
  MapMode = 2
FEATURE [App::DocumentObjectGroup] Constraints
FEATURE [App::FeaturePython] Variables  # WARN: FeaturePython — macro-defined, semantics opaque (R4)
  Type = App::PropertyContainer
FEATURE [App::DocumentObjectGroup] Configurations
FEATURE [App::Link] M5_rod
  AttachedBy = #bottom
  AttachedTo = Parent Assembly#LCS_Origin
  LinkedObject = -> <external ../../Part/Purchase/M5_rod.FCStd>#Part
  SolverId = Asm4EE
  expr: Placement = LCS_Origin.Placement * AttachmentOffset * M5_rod#bottom.Placement ^ -1
FEATURE [Part::FeaturePython] Nut  label="M5-Nut"  # WARN: FeaturePython — macro-defined, semantics opaque (R4)
  Diameter = 3
  Invert = false
  LeftHanded = false
  MatchOuter = false
  Offset = 4
  OffsetAngle = 0
  Placement = pos=(0,6e-16,10) rot=(1,0,0;3.14159rad)
  Thread = false
  Type = 21
FEATURE [App::Part] Assembly  label="Assy_M5_rod"
  AssemblyType = Part::Link
  Group = -> [LCS_Origin,Constraints,Variables,Configurations,M5_rod,Nut]
  Origin = -> Origin
  Type = Assembly
